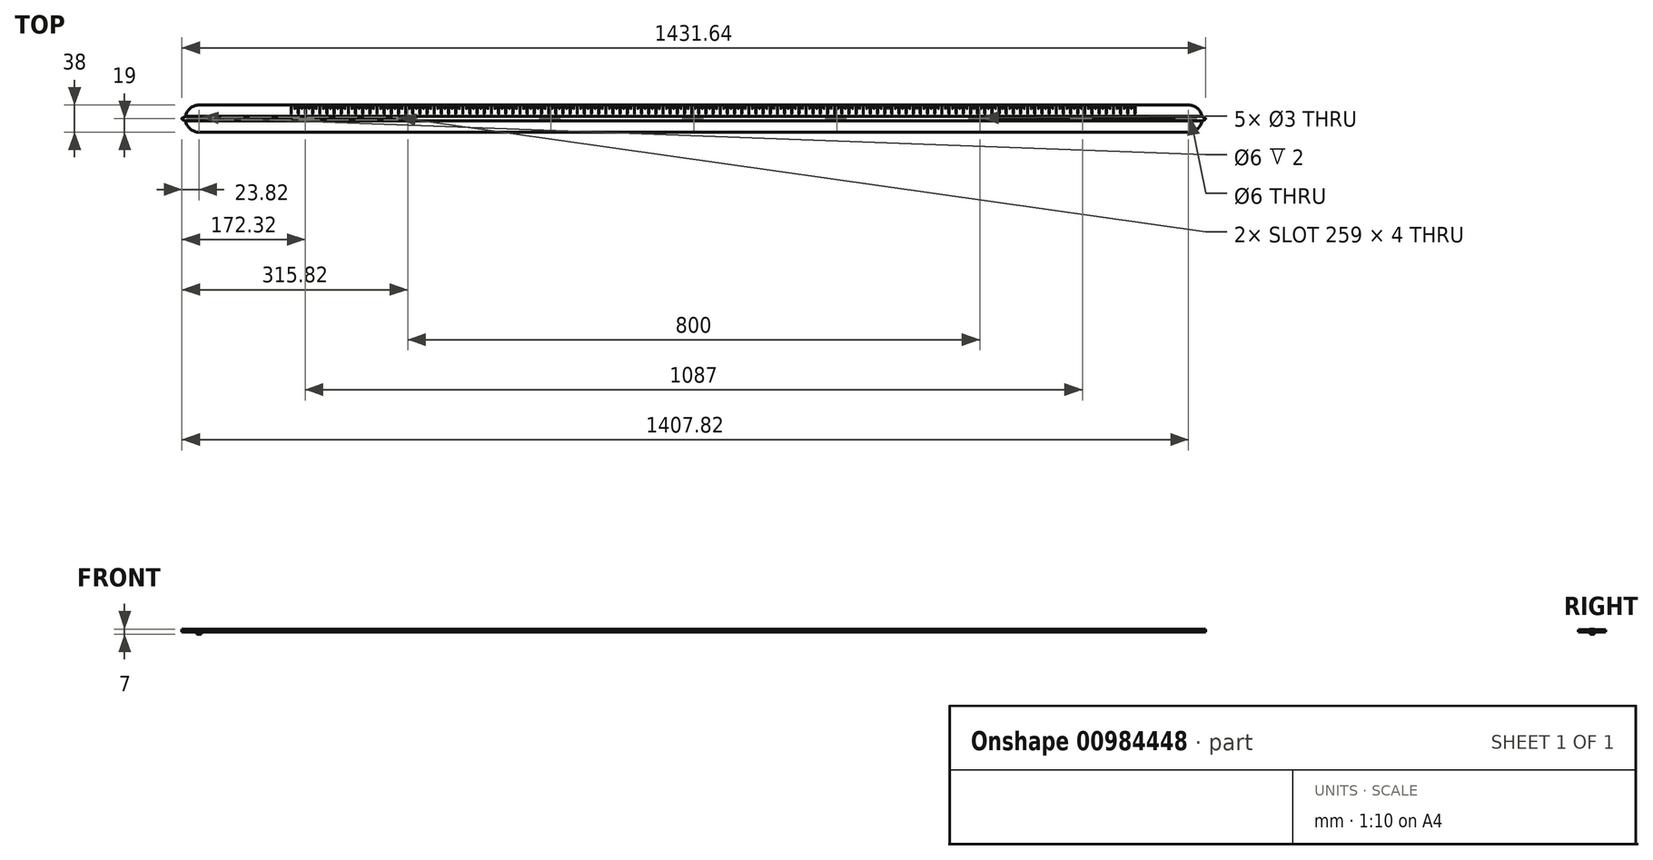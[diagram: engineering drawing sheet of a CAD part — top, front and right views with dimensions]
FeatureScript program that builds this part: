
annotation { "Feature Type Name" : "Feature", "Feature Type Description" : "" }
export const myFeature = defineFeature(function(context is Context, id is Id, definition is map)
    precondition{}
    {
        {
            var Q0;
            Q0=qCreatedBy(makeId("Right.planeOp"),FACE);
            var sketch = newSketch(context, id + "F0", { "sketchPlane" : qUnion([Q0])});
            skLineSegment(sketch, "E0", {"start": v(0, 0) * mm, "end": v(-19, 0) * mm, "construction": true});
            skLineSegment(sketch, "E1", {"start": v(-19, 0) * mm, "end": v(19, 0) * mm});
            skLineSegment(sketch, "E2", {"start": v(19, 0) * mm, "end": v(19, 3) * mm});
            skLineSegment(sketch, "E3", {"start": v(19, 3) * mm, "end": v(3.25, 3) * mm});
            skLineSegment(sketch, "E4", {"start": v(3.25, 3) * mm, "end": v(3.25, 4) * mm, "construction": true});
            skLineSegment(sketch, "E5", {"start": v(3.25, 4) * mm, "end": v(0, 4) * mm, "construction": true});
            skLineSegment(sketch, "E6", {"start": v(0, 4) * mm, "end": v(3, 4) * mm, "construction": true});
            skLineSegment(sketch, "E7", {"start": v(3, 4) * mm, "end": v(3.25, 3) * mm});
            skLineSegment(sketch, "E8", {"start": v(3, 4) * mm, "end": v(-3, 4) * mm});
            skLineSegment(sketch, "E9", {"start": v(-19, 0) * mm, "end": v(-19, 3) * mm});
            skLineSegment(sketch, "E10", {"start": v(-19, 3) * mm, "end": v(-3.25, 3) * mm});
            skLineSegment(sketch, "E11", {"start": v(-3.25, 3) * mm, "end": v(-3, 4) * mm});
            skSolve(sketch);
        }
        {
            var Q0;
            Q0=makeQuery(id+"F0.imprint","IMPRINT",FACE,{"disambiguationData":[TD([[makeQuery(id+"F0.imprint","IMPRINT",EDGE,{"derivedFrom":sQuery(id+"F0.wireOp",EDGE,"E1")}),1.0]])]});
            extrude(context, id + "F1", {"entities" : qUnion([Q0]), "depth" : 1280 * mm, "offsetDistance" : 25 * mm, "hasSecondDirection" : true, "secondDirectionOppositeDirection" : true, "secondDirectionDepth" : (129 + 19 + 6) * mm});
        }
        {
            var Q0;
            Q0=qCreatedBy(makeId("Top.planeOp"),FACE);
            var sketch = newSketch(context, id + "F2", { "sketchPlane" : qUnion([Q0])});
            skLineSegment(sketch, "E12.0.0", {"start": v(-154, 3) * mm, "end": v(-154, -3) * mm, "construction": true});
            skLineSegment(sketch, "E12.0.1", {"start": v(-154, -3) * mm, "end": v(1280, -3) * mm, "construction": true});
            skLineSegment(sketch, "E12.0.2", {"start": v(1280, -3) * mm, "end": v(1280, 3) * mm, "construction": true});
            skLineSegment(sketch, "E12.0.3", {"start": v(1280, 3) * mm, "end": v(-154, 3) * mm, "construction": true});
            skLineSegment(sketch, "E13", {"start": v(563, 3) * mm, "end": v(563, -3) * mm});
            skSolve(sketch);
        }
        {
            var Q0;
            Q0=qCreatedBy(makeId("Top.planeOp"),FACE);
            var sketch = newSketch(context, id + "F3", { "sketchPlane" : qUnion([Q0])});
            skLineSegment(sketch, "E14", {"start": v(0, 0) * mm, "end": v(-129, 0) * mm, "construction": true});
            skCircle(sketch, "E15", {"center": v(-129, 0) * mm, "radius": 3 * mm});
            skCircle(sketch, "E16.MirrorC", {"center": v(1255, 0) * mm, "radius": 3 * mm});
            skLineSegment(sketch, "E17.MirrorCS", {"start": v(1126, 0) * mm, "end": v(1255, 0) * mm, "construction": true});
            skSolve(sketch);
        }
        {
            var Q0;
            Q0 = qSketchRegion(id + "F3", true);
            extrude(context, id + "F4", {"entities" : qUnion([Q0]), "operationType" : NewBodyOperationType.REMOVE, "depth" : 25 * mm, "offsetDistance" : 25 * mm});
        }
        {
            var Q0;
            Q0=qCreatedBy(makeId("Top.planeOp"),FACE);
            var sketch = newSketch(context, id + "F5", { "sketchPlane" : qUnion([Q0])});
            skArc(sketch, "E18.0", {"start": v(-129, 3) * mm, "mid": v(-132, 0) * mm, "end": v(-129, -3) * mm, "construction": true});
            skArc(sketch, "E19.0", {"start": v(-129, -3) * mm, "mid": v(-126, 0) * mm, "end": v(-129, 3) * mm, "construction": true});
            skLineSegment(sketch, "E20", {"start": v(-129, 0) * mm, "end": v(-108, 0) * mm, "construction": true});
            skPoint(sketch, "E20.endSnap0", {"position": v(-126, 0) * mm});
            skLineSegment(sketch, "E21", {"start": v(-108, 0) * mm, "end": v(147, 0) * mm});
            skArc(sketch, "E22.0.startCap", {"start": v(-108, -2) * mm, "mid": v(-110, 0) * mm, "end": v(-108, 2) * mm});
            skArc(sketch, "E22.0.endCap", {"start": v(147, 2) * mm, "mid": v(149, 0) * mm, "end": v(147, -2) * mm});
            skLineSegment(sketch, "E22.0.left", {"start": v(-108, 2) * mm, "end": v(147, 2) * mm});
            skLineSegment(sketch, "E22.0.right", {"start": v(-108, -2) * mm, "end": v(147, -2) * mm});
            skArc(sketch, "E23.MirrorCS", {"start": v(1255, -3) * mm, "mid": v(1252, 0) * mm, "end": v(1255, 3) * mm, "construction": true});
            skArc(sketch, "E24.MirrorCS", {"start": v(1234, -2) * mm, "mid": v(1236, 0) * mm, "end": v(1234, 2) * mm});
            skArc(sketch, "E25.MirrorCS", {"start": v(1255, 3) * mm, "mid": v(1258, 0) * mm, "end": v(1255, -3) * mm, "construction": true});
            skPoint(sketch, "E26.MirrorP", {"position": v(1252, 0) * mm});
            skLineSegment(sketch, "E27.MirrorCS", {"start": v(1255, 0) * mm, "end": v(1234, 0) * mm, "construction": true});
            skArc(sketch, "E28.MirrorCS", {"start": v(979, 2) * mm, "mid": v(977, 0) * mm, "end": v(979, -2) * mm});
            skLineSegment(sketch, "E29.MirrorCS", {"start": v(1234, 0) * mm, "end": v(979, 0) * mm});
            skLineSegment(sketch, "E30.MirrorCS", {"start": v(1234, -2) * mm, "end": v(979, -2) * mm});
            skLineSegment(sketch, "E31.MirrorCS", {"start": v(1234, 2) * mm, "end": v(979, 2) * mm});
            skSolve(sketch);
        }
        {
            var Q0;
            Q0 = qSketchRegion(id + "F5", true);
            extrude(context, id + "F6", {"entities" : qUnion([Q0]), "operationType" : NewBodyOperationType.REMOVE, "depth" : 25 * mm, "offsetDistance" : 25 * mm});
        }
        {
            var Q0;
            Q0=qCreatedBy(makeId("Top.planeOp"),FACE);
            var sketch = newSketch(context, id + "F7", { "sketchPlane" : qUnion([Q0])});
            skArc(sketch, "E32.0", {"start": v(-129, 3) * mm, "mid": v(-132, 0) * mm, "end": v(-129, -3) * mm, "construction": true});
            skArc(sketch, "E33", {"start": v(-129, 19) * mm, "mid": v(-140.88, 14.83) * mm, "end": v(-147.54, 4.15) * mm});
            skLineSegment(sketch, "E34.0", {"start": v(1280, 3.25) * mm, "end": v(-154, 3.25) * mm, "construction": true});
            skLineSegment(sketch, "E35.0", {"start": v(1280, -3.25) * mm, "end": v(-154, -3.25) * mm, "construction": true});
            skLineSegment(sketch, "E36.0", {"start": v(-154, 3) * mm, "end": v(-154, -3) * mm, "construction": true});
            skLineSegment(sketch, "E37", {"start": v(-152.28, 0.89) * mm, "end": v(-148.57, 2.8) * mm});
            skLineSegment(sketch, "E38.bottom", {"start": v(-158.98, 22.26) * mm, "end": v(-129, 22.26) * mm});
            skLineSegment(sketch, "E38.top", {"start": v(-158.98, -20.88) * mm, "end": v(-129, -20.88) * mm});
            skLineSegment(sketch, "E38.left", {"start": v(-158.98, 22.26) * mm, "end": v(-158.98, -20.88) * mm});
            skLineSegment(sketch, "E38.right", {"start": v(-129, 22.26) * mm, "end": v(-129, 19) * mm});
            skLineSegment(sketch, "E39.trimOffspring", {"start": v(-129, -19) * mm, "end": v(-129, -20.88) * mm});
            skLineSegment(sketch, "E40.trimOffspring", {"start": v(-129, -3) * mm, "end": v(-129, -3.25) * mm});
            skLineSegment(sketch, "E41.trimOffspring", {"start": v(-129, 3.25) * mm, "end": v(-129, 3) * mm});
            skLineSegment(sketch, "E42", {"start": v(-152.28, -0.89) * mm, "end": v(-148.57, -2.8) * mm});
            skArc(sketch, "E43.trimOffspring", {"start": v(-147.54, -4.15) * mm, "mid": v(-140.88, -14.83) * mm, "end": v(-129, -19) * mm});
            skLineSegment(sketch, "E44", {"start": v(-129, 0) * mm, "end": v(-154, 0) * mm, "construction": true});
            skPoint(sketch, "E45.visualSharp", {"position": v(-147.72, 3.25) * mm});
            skArc(sketch, "E45.filletArc", {"start": v(-148.57, 2.8) * mm, "mid": v(-147.9, 3.36) * mm, "end": v(-147.54, 4.15) * mm});
            skPoint(sketch, "E46.visualSharp", {"position": v(-147.72, -3.25) * mm});
            skArc(sketch, "E46.filletArc", {"start": v(-147.54, -4.15) * mm, "mid": v(-147.9, -3.36) * mm, "end": v(-148.57, -2.8) * mm});
            skPoint(sketch, "E47.visualSharp", {"position": v(-154, 0) * mm});
            skArc(sketch, "E47.filletArc", {"start": v(-152.28, 0.89) * mm, "mid": v(-152.82, 0) * mm, "end": v(-152.28, -0.89) * mm});
            skArc(sketch, "E48.MirrorCS", {"start": v(1278.28, 0.89) * mm, "mid": v(1278.82, 0) * mm, "end": v(1278.28, -0.89) * mm});
            skArc(sketch, "E49.MirrorCS", {"start": v(1274.57, 2.8) * mm, "mid": v(1273.9, 3.36) * mm, "end": v(1273.54, 4.15) * mm});
            skLineSegment(sketch, "E50.MirrorCS", {"start": v(1278.28, -0.89) * mm, "end": v(1274.57, -2.8) * mm});
            skLineSegment(sketch, "E51.MirrorCS", {"start": v(1278.28, 0.89) * mm, "end": v(1274.57, 2.8) * mm});
            skLineSegment(sketch, "E52.MirrorCS", {"start": v(1280, 3) * mm, "end": v(1280, -3) * mm, "construction": true});
            skArc(sketch, "E53.MirrorCS", {"start": v(1273.54, -4.15) * mm, "mid": v(1273.9, -3.36) * mm, "end": v(1274.57, -2.8) * mm});
            skLineSegment(sketch, "E54.MirrorCS", {"start": v(1255, 3.25) * mm, "end": v(1255, 3) * mm});
            skLineSegment(sketch, "E55.MirrorCS", {"start": v(1255, -3) * mm, "end": v(1255, -3.25) * mm});
            skLineSegment(sketch, "E56.MirrorCS", {"start": v(1255, 0) * mm, "end": v(1280, 0) * mm, "construction": true});
            skArc(sketch, "E57.MirrorCS", {"start": v(1255, 3) * mm, "mid": v(1258, 0) * mm, "end": v(1255, -3) * mm, "construction": true});
            skLineSegment(sketch, "E58.MirrorCS", {"start": v(1255, -19) * mm, "end": v(1255, -20.88) * mm});
            skArc(sketch, "E59.MirrorCS", {"start": v(1273.54, -4.15) * mm, "mid": v(1266.88, -14.83) * mm, "end": v(1255, -19) * mm});
            skLineSegment(sketch, "E60.MirrorCS", {"start": v(1255, 22.26) * mm, "end": v(1255, 19) * mm});
            skArc(sketch, "E61.MirrorCS", {"start": v(1255, 19) * mm, "mid": v(1266.88, 14.83) * mm, "end": v(1273.54, 4.15) * mm});
            skLineSegment(sketch, "E62.MirrorCS", {"start": v(1284.98, 22.26) * mm, "end": v(1284.98, -20.88) * mm});
            skLineSegment(sketch, "E63.MirrorCS", {"start": v(1284.98, -20.88) * mm, "end": v(1255, -20.88) * mm});
            skLineSegment(sketch, "E64.MirrorCS", {"start": v(1284.98, 22.26) * mm, "end": v(1255, 22.26) * mm});
            skPoint(sketch, "E65.MirrorP", {"position": v(1273.72, 3.25) * mm});
            skPoint(sketch, "E66.MirrorP", {"position": v(1273.72, -3.25) * mm});
            skPoint(sketch, "E67.MirrorP", {"position": v(1280, 0) * mm});
            skSolve(sketch);
        }
        {
            var Q0;
            Q0 = qSketchRegion(id + "F7", true);
            extrude(context, id + "F8", {"entities" : qUnion([Q0]), "operationType" : NewBodyOperationType.REMOVE, "depth" : 25 * mm, "offsetDistance" : 25 * mm});
        }
        {
            var Q0;
            Q0=qCreatedBy(makeId("Top.planeOp"),FACE);
            var sketch = newSketch(context, id + "F9", { "sketchPlane" : qUnion([Q0])});
            skArc(sketch, "E68.0", {"start": v(147, 2) * mm, "mid": v(149, 0) * mm, "end": v(147, -2) * mm, "construction": true});
            skArc(sketch, "E69.0", {"start": v(979, 2) * mm, "mid": v(977, 0) * mm, "end": v(979, -2) * mm, "construction": true});
            skLineSegment(sketch, "E70", {"start": v(147, 0) * mm, "end": v(979, 0) * mm, "construction": true});
            skCircle(sketch, "E71", {"center": v(563, 0) * mm, "radius": 1.5 * mm});
            skCircle(sketch, "E72.1.0.0", {"center": v(763, 0) * mm, "radius": 1.5 * mm});
            skCircle(sketch, "E72.2.0.0", {"center": v(963, 0) * mm, "radius": 1.5 * mm});
            skLineSegment(sketch, "E72.direction1", {"start": v(563, 0) * mm, "end": v(763, 0) * mm, "construction": true});
            skCircle(sketch, "E73.1.0.0", {"center": v(363, 0) * mm, "radius": 1.5 * mm});
            skCircle(sketch, "E73.2.0.0", {"center": v(163, 0) * mm, "radius": 1.5 * mm});
            skLineSegment(sketch, "E73.direction1", {"start": v(563, 0) * mm, "end": v(363, 0) * mm, "construction": true});
            skSolve(sketch);
        }
        {
            var Q0;
            Q0 = qSketchRegion(id + "F9", true);
            extrude(context, id + "F10", {"entities" : qUnion([Q0]), "operationType" : NewBodyOperationType.REMOVE, "depth" : 25 * mm, "offsetDistance" : 25 * mm});
        }
        {
            var Q0;
            Q0=makeQuery(id+"F1.opExtrude","SWEPT_FACE",FACE,{"disambiguationData":[OSD([sQuery(id+"F0.wireOp",EDGE,"E3")])]});
            var sketch = newSketch(context, id + "F11", { "sketchPlane" : qUnion([Q0])});
            skLineSegment(sketch, "E74", {"start": v(0, 0) * mm, "end": v(0, 19) * mm, "construction": true});
            skLineSegment(sketch, "E75", {"start": v(0, 19) * mm, "end": v(0, 7) * mm});
            skArc(sketch, "E76.0.startCap", {"start": v(-0.25, 19) * mm, "mid": v(0, 19.25) * mm, "end": v(0.25, 19) * mm});
            skArc(sketch, "E76.0.endCap", {"start": v(0.25, 7) * mm, "mid": v(0, 6.75) * mm, "end": v(-0.25, 7) * mm});
            skLineSegment(sketch, "E76.0.left", {"start": v(0.25, 19) * mm, "end": v(0.25, 7) * mm});
            skLineSegment(sketch, "E76.0.right", {"start": v(-0.25, 19) * mm, "end": v(-0.25, 7) * mm});
            skLineSegment(sketch, "E77.1.0.0", {"start": v(10.25, 19) * mm, "end": v(10.25, 7) * mm});
            skLineSegment(sketch, "E77.1.0.1", {"start": v(9.75, 19) * mm, "end": v(9.75, 7) * mm});
            skLineSegment(sketch, "E77.1.0.2", {"start": v(10, 19) * mm, "end": v(10, 7) * mm});
            skArc(sketch, "E77.1.0.3", {"start": v(10.25, 7) * mm, "mid": v(10, 6.75) * mm, "end": v(9.75, 7) * mm});
            skArc(sketch, "E77.1.0.4", {"start": v(9.75, 19) * mm, "mid": v(10, 19.25) * mm, "end": v(10.25, 19) * mm});
            skLineSegment(sketch, "E77.2.0.0", {"start": v(20.25, 19) * mm, "end": v(20.25, 7) * mm});
            skLineSegment(sketch, "E77.2.0.1", {"start": v(19.75, 19) * mm, "end": v(19.75, 7) * mm});
            skLineSegment(sketch, "E77.2.0.2", {"start": v(20, 19) * mm, "end": v(20, 7) * mm});
            skArc(sketch, "E77.2.0.3", {"start": v(20.25, 7) * mm, "mid": v(20, 6.75) * mm, "end": v(19.75, 7) * mm});
            skArc(sketch, "E77.2.0.4", {"start": v(19.75, 19) * mm, "mid": v(20, 19.25) * mm, "end": v(20.25, 19) * mm});
            skLineSegment(sketch, "E77.3.0.0", {"start": v(30.25, 19) * mm, "end": v(30.25, 7) * mm});
            skLineSegment(sketch, "E77.3.0.1", {"start": v(29.75, 19) * mm, "end": v(29.75, 7) * mm});
            skLineSegment(sketch, "E77.3.0.2", {"start": v(30, 19) * mm, "end": v(30, 7) * mm});
            skArc(sketch, "E77.3.0.3", {"start": v(30.25, 7) * mm, "mid": v(30, 6.75) * mm, "end": v(29.75, 7) * mm});
            skArc(sketch, "E77.3.0.4", {"start": v(29.75, 19) * mm, "mid": v(30, 19.25) * mm, "end": v(30.25, 19) * mm});
            skLineSegment(sketch, "E77.4.0.0", {"start": v(40.25, 19) * mm, "end": v(40.25, 7) * mm});
            skLineSegment(sketch, "E77.4.0.1", {"start": v(39.75, 19) * mm, "end": v(39.75, 7) * mm});
            skLineSegment(sketch, "E77.4.0.2", {"start": v(40, 19) * mm, "end": v(40, 7) * mm});
            skArc(sketch, "E77.4.0.3", {"start": v(40.25, 7) * mm, "mid": v(40, 6.75) * mm, "end": v(39.75, 7) * mm});
            skArc(sketch, "E77.4.0.4", {"start": v(39.75, 19) * mm, "mid": v(40, 19.25) * mm, "end": v(40.25, 19) * mm});
            skLineSegment(sketch, "E77.5.0.0", {"start": v(50.25, 19) * mm, "end": v(50.25, 7) * mm});
            skLineSegment(sketch, "E77.5.0.1", {"start": v(49.75, 19) * mm, "end": v(49.75, 7) * mm});
            skLineSegment(sketch, "E77.5.0.2", {"start": v(50, 19) * mm, "end": v(50, 7) * mm});
            skArc(sketch, "E77.5.0.3", {"start": v(50.25, 7) * mm, "mid": v(50, 6.75) * mm, "end": v(49.75, 7) * mm});
            skArc(sketch, "E77.5.0.4", {"start": v(49.75, 19) * mm, "mid": v(50, 19.25) * mm, "end": v(50.25, 19) * mm});
            skLineSegment(sketch, "E77.6.0.0", {"start": v(60.25, 19) * mm, "end": v(60.25, 7) * mm});
            skLineSegment(sketch, "E77.6.0.1", {"start": v(59.75, 19) * mm, "end": v(59.75, 7) * mm});
            skLineSegment(sketch, "E77.6.0.2", {"start": v(60, 19) * mm, "end": v(60, 7) * mm});
            skArc(sketch, "E77.6.0.3", {"start": v(60.25, 7) * mm, "mid": v(60, 6.75) * mm, "end": v(59.75, 7) * mm});
            skArc(sketch, "E77.6.0.4", {"start": v(59.75, 19) * mm, "mid": v(60, 19.25) * mm, "end": v(60.25, 19) * mm});
            skLineSegment(sketch, "E77.7.0.0", {"start": v(70.25, 19) * mm, "end": v(70.25, 7) * mm});
            skLineSegment(sketch, "E77.7.0.1", {"start": v(69.75, 19) * mm, "end": v(69.75, 7) * mm});
            skLineSegment(sketch, "E77.7.0.2", {"start": v(70, 19) * mm, "end": v(70, 7) * mm});
            skArc(sketch, "E77.7.0.3", {"start": v(70.25, 7) * mm, "mid": v(70, 6.75) * mm, "end": v(69.75, 7) * mm});
            skArc(sketch, "E77.7.0.4", {"start": v(69.75, 19) * mm, "mid": v(70, 19.25) * mm, "end": v(70.25, 19) * mm});
            skLineSegment(sketch, "E77.8.0.0", {"start": v(80.25, 19) * mm, "end": v(80.25, 7) * mm});
            skLineSegment(sketch, "E77.8.0.1", {"start": v(79.75, 19) * mm, "end": v(79.75, 7) * mm});
            skLineSegment(sketch, "E77.8.0.2", {"start": v(80, 19) * mm, "end": v(80, 7) * mm});
            skArc(sketch, "E77.8.0.3", {"start": v(80.25, 7) * mm, "mid": v(80, 6.75) * mm, "end": v(79.75, 7) * mm});
            skArc(sketch, "E77.8.0.4", {"start": v(79.75, 19) * mm, "mid": v(80, 19.25) * mm, "end": v(80.25, 19) * mm});
            skLineSegment(sketch, "E77.9.0.0", {"start": v(90.25, 19) * mm, "end": v(90.25, 7) * mm});
            skLineSegment(sketch, "E77.9.0.1", {"start": v(89.75, 19) * mm, "end": v(89.75, 7) * mm});
            skLineSegment(sketch, "E77.9.0.2", {"start": v(90, 19) * mm, "end": v(90, 7) * mm});
            skArc(sketch, "E77.9.0.3", {"start": v(90.25, 7) * mm, "mid": v(90, 6.75) * mm, "end": v(89.75, 7) * mm});
            skArc(sketch, "E77.9.0.4", {"start": v(89.75, 19) * mm, "mid": v(90, 19.25) * mm, "end": v(90.25, 19) * mm});
            skLineSegment(sketch, "E77.10.0.0", {"start": v(100.25, 19) * mm, "end": v(100.25, 7) * mm});
            skLineSegment(sketch, "E77.10.0.1", {"start": v(99.75, 19) * mm, "end": v(99.75, 7) * mm});
            skLineSegment(sketch, "E77.10.0.2", {"start": v(100, 19) * mm, "end": v(100, 7) * mm});
            skArc(sketch, "E77.10.0.3", {"start": v(100.25, 7) * mm, "mid": v(100, 6.75) * mm, "end": v(99.75, 7) * mm});
            skArc(sketch, "E77.10.0.4", {"start": v(99.75, 19) * mm, "mid": v(100, 19.25) * mm, "end": v(100.25, 19) * mm});
            skLineSegment(sketch, "E77.11.0.0", {"start": v(110.25, 19) * mm, "end": v(110.25, 7) * mm});
            skLineSegment(sketch, "E77.11.0.1", {"start": v(109.75, 19) * mm, "end": v(109.75, 7) * mm});
            skLineSegment(sketch, "E77.11.0.2", {"start": v(110, 19) * mm, "end": v(110, 7) * mm});
            skArc(sketch, "E77.11.0.3", {"start": v(110.25, 7) * mm, "mid": v(110, 6.75) * mm, "end": v(109.75, 7) * mm});
            skArc(sketch, "E77.11.0.4", {"start": v(109.75, 19) * mm, "mid": v(110, 19.25) * mm, "end": v(110.25, 19) * mm});
            skLineSegment(sketch, "E77.12.0.0", {"start": v(120.25, 19) * mm, "end": v(120.25, 7) * mm});
            skLineSegment(sketch, "E77.12.0.1", {"start": v(119.75, 19) * mm, "end": v(119.75, 7) * mm});
            skLineSegment(sketch, "E77.12.0.2", {"start": v(120, 19) * mm, "end": v(120, 7) * mm});
            skArc(sketch, "E77.12.0.3", {"start": v(120.25, 7) * mm, "mid": v(120, 6.75) * mm, "end": v(119.75, 7) * mm});
            skArc(sketch, "E77.12.0.4", {"start": v(119.75, 19) * mm, "mid": v(120, 19.25) * mm, "end": v(120.25, 19) * mm});
            skLineSegment(sketch, "E77.13.0.0", {"start": v(130.25, 19) * mm, "end": v(130.25, 7) * mm});
            skLineSegment(sketch, "E77.13.0.1", {"start": v(129.75, 19) * mm, "end": v(129.75, 7) * mm});
            skLineSegment(sketch, "E77.13.0.2", {"start": v(130, 19) * mm, "end": v(130, 7) * mm});
            skArc(sketch, "E77.13.0.3", {"start": v(130.25, 7) * mm, "mid": v(130, 6.75) * mm, "end": v(129.75, 7) * mm});
            skArc(sketch, "E77.13.0.4", {"start": v(129.75, 19) * mm, "mid": v(130, 19.25) * mm, "end": v(130.25, 19) * mm});
            skLineSegment(sketch, "E77.14.0.0", {"start": v(140.25, 19) * mm, "end": v(140.25, 7) * mm});
            skLineSegment(sketch, "E77.14.0.1", {"start": v(139.75, 19) * mm, "end": v(139.75, 7) * mm});
            skLineSegment(sketch, "E77.14.0.2", {"start": v(140, 19) * mm, "end": v(140, 7) * mm});
            skArc(sketch, "E77.14.0.3", {"start": v(140.25, 7) * mm, "mid": v(140, 6.75) * mm, "end": v(139.75, 7) * mm});
            skArc(sketch, "E77.14.0.4", {"start": v(139.75, 19) * mm, "mid": v(140, 19.25) * mm, "end": v(140.25, 19) * mm});
            skLineSegment(sketch, "E77.15.0.0", {"start": v(150.25, 19) * mm, "end": v(150.25, 7) * mm});
            skLineSegment(sketch, "E77.15.0.1", {"start": v(149.75, 19) * mm, "end": v(149.75, 7) * mm});
            skLineSegment(sketch, "E77.15.0.2", {"start": v(150, 19) * mm, "end": v(150, 7) * mm});
            skArc(sketch, "E77.15.0.3", {"start": v(150.25, 7) * mm, "mid": v(150, 6.75) * mm, "end": v(149.75, 7) * mm});
            skArc(sketch, "E77.15.0.4", {"start": v(149.75, 19) * mm, "mid": v(150, 19.25) * mm, "end": v(150.25, 19) * mm});
            skLineSegment(sketch, "E77.16.0.0", {"start": v(160.25, 19) * mm, "end": v(160.25, 7) * mm});
            skLineSegment(sketch, "E77.16.0.1", {"start": v(159.75, 19) * mm, "end": v(159.75, 7) * mm});
            skLineSegment(sketch, "E77.16.0.2", {"start": v(160, 19) * mm, "end": v(160, 7) * mm});
            skArc(sketch, "E77.16.0.3", {"start": v(160.25, 7) * mm, "mid": v(160, 6.75) * mm, "end": v(159.75, 7) * mm});
            skArc(sketch, "E77.16.0.4", {"start": v(159.75, 19) * mm, "mid": v(160, 19.25) * mm, "end": v(160.25, 19) * mm});
            skLineSegment(sketch, "E77.17.0.0", {"start": v(170.25, 19) * mm, "end": v(170.25, 7) * mm});
            skLineSegment(sketch, "E77.17.0.1", {"start": v(169.75, 19) * mm, "end": v(169.75, 7) * mm});
            skLineSegment(sketch, "E77.17.0.2", {"start": v(170, 19) * mm, "end": v(170, 7) * mm});
            skArc(sketch, "E77.17.0.3", {"start": v(170.25, 7) * mm, "mid": v(170, 6.75) * mm, "end": v(169.75, 7) * mm});
            skArc(sketch, "E77.17.0.4", {"start": v(169.75, 19) * mm, "mid": v(170, 19.25) * mm, "end": v(170.25, 19) * mm});
            skLineSegment(sketch, "E77.18.0.0", {"start": v(180.25, 19) * mm, "end": v(180.25, 7) * mm});
            skLineSegment(sketch, "E77.18.0.1", {"start": v(179.75, 19) * mm, "end": v(179.75, 7) * mm});
            skLineSegment(sketch, "E77.18.0.2", {"start": v(180, 19) * mm, "end": v(180, 7) * mm});
            skArc(sketch, "E77.18.0.3", {"start": v(180.25, 7) * mm, "mid": v(180, 6.75) * mm, "end": v(179.75, 7) * mm});
            skArc(sketch, "E77.18.0.4", {"start": v(179.75, 19) * mm, "mid": v(180, 19.25) * mm, "end": v(180.25, 19) * mm});
            skLineSegment(sketch, "E77.19.0.0", {"start": v(190.25, 19) * mm, "end": v(190.25, 7) * mm});
            skLineSegment(sketch, "E77.19.0.1", {"start": v(189.75, 19) * mm, "end": v(189.75, 7) * mm});
            skLineSegment(sketch, "E77.19.0.2", {"start": v(190, 19) * mm, "end": v(190, 7) * mm});
            skArc(sketch, "E77.19.0.3", {"start": v(190.25, 7) * mm, "mid": v(190, 6.75) * mm, "end": v(189.75, 7) * mm});
            skArc(sketch, "E77.19.0.4", {"start": v(189.75, 19) * mm, "mid": v(190, 19.25) * mm, "end": v(190.25, 19) * mm});
            skLineSegment(sketch, "E77.20.0.0", {"start": v(200.25, 19) * mm, "end": v(200.25, 7) * mm});
            skLineSegment(sketch, "E77.20.0.1", {"start": v(199.75, 19) * mm, "end": v(199.75, 7) * mm});
            skLineSegment(sketch, "E77.20.0.2", {"start": v(200, 19) * mm, "end": v(200, 7) * mm});
            skArc(sketch, "E77.20.0.3", {"start": v(200.25, 7) * mm, "mid": v(200, 6.75) * mm, "end": v(199.75, 7) * mm});
            skArc(sketch, "E77.20.0.4", {"start": v(199.75, 19) * mm, "mid": v(200, 19.25) * mm, "end": v(200.25, 19) * mm});
            skLineSegment(sketch, "E77.21.0.0", {"start": v(210.25, 19) * mm, "end": v(210.25, 7) * mm});
            skLineSegment(sketch, "E77.21.0.1", {"start": v(209.75, 19) * mm, "end": v(209.75, 7) * mm});
            skLineSegment(sketch, "E77.21.0.2", {"start": v(210, 19) * mm, "end": v(210, 7) * mm});
            skArc(sketch, "E77.21.0.3", {"start": v(210.25, 7) * mm, "mid": v(210, 6.75) * mm, "end": v(209.75, 7) * mm});
            skArc(sketch, "E77.21.0.4", {"start": v(209.75, 19) * mm, "mid": v(210, 19.25) * mm, "end": v(210.25, 19) * mm});
            skLineSegment(sketch, "E77.22.0.0", {"start": v(220.25, 19) * mm, "end": v(220.25, 7) * mm});
            skLineSegment(sketch, "E77.22.0.1", {"start": v(219.75, 19) * mm, "end": v(219.75, 7) * mm});
            skLineSegment(sketch, "E77.22.0.2", {"start": v(220, 19) * mm, "end": v(220, 7) * mm});
            skArc(sketch, "E77.22.0.3", {"start": v(220.25, 7) * mm, "mid": v(220, 6.75) * mm, "end": v(219.75, 7) * mm});
            skArc(sketch, "E77.22.0.4", {"start": v(219.75, 19) * mm, "mid": v(220, 19.25) * mm, "end": v(220.25, 19) * mm});
            skLineSegment(sketch, "E77.23.0.0", {"start": v(230.25, 19) * mm, "end": v(230.25, 7) * mm});
            skLineSegment(sketch, "E77.23.0.1", {"start": v(229.75, 19) * mm, "end": v(229.75, 7) * mm});
            skLineSegment(sketch, "E77.23.0.2", {"start": v(230, 19) * mm, "end": v(230, 7) * mm});
            skArc(sketch, "E77.23.0.3", {"start": v(230.25, 7) * mm, "mid": v(230, 6.75) * mm, "end": v(229.75, 7) * mm});
            skArc(sketch, "E77.23.0.4", {"start": v(229.75, 19) * mm, "mid": v(230, 19.25) * mm, "end": v(230.25, 19) * mm});
            skLineSegment(sketch, "E77.24.0.0", {"start": v(240.25, 19) * mm, "end": v(240.25, 7) * mm});
            skLineSegment(sketch, "E77.24.0.1", {"start": v(239.75, 19) * mm, "end": v(239.75, 7) * mm});
            skLineSegment(sketch, "E77.24.0.2", {"start": v(240, 19) * mm, "end": v(240, 7) * mm});
            skArc(sketch, "E77.24.0.3", {"start": v(240.25, 7) * mm, "mid": v(240, 6.75) * mm, "end": v(239.75, 7) * mm});
            skArc(sketch, "E77.24.0.4", {"start": v(239.75, 19) * mm, "mid": v(240, 19.25) * mm, "end": v(240.25, 19) * mm});
            skLineSegment(sketch, "E77.25.0.0", {"start": v(250.25, 19) * mm, "end": v(250.25, 7) * mm});
            skLineSegment(sketch, "E77.25.0.1", {"start": v(249.75, 19) * mm, "end": v(249.75, 7) * mm});
            skLineSegment(sketch, "E77.25.0.2", {"start": v(250, 19) * mm, "end": v(250, 7) * mm});
            skArc(sketch, "E77.25.0.3", {"start": v(250.25, 7) * mm, "mid": v(250, 6.75) * mm, "end": v(249.75, 7) * mm});
            skArc(sketch, "E77.25.0.4", {"start": v(249.75, 19) * mm, "mid": v(250, 19.25) * mm, "end": v(250.25, 19) * mm});
            skLineSegment(sketch, "E77.26.0.0", {"start": v(260.25, 19) * mm, "end": v(260.25, 7) * mm});
            skLineSegment(sketch, "E77.26.0.1", {"start": v(259.75, 19) * mm, "end": v(259.75, 7) * mm});
            skLineSegment(sketch, "E77.26.0.2", {"start": v(260, 19) * mm, "end": v(260, 7) * mm});
            skArc(sketch, "E77.26.0.3", {"start": v(260.25, 7) * mm, "mid": v(260, 6.75) * mm, "end": v(259.75, 7) * mm});
            skArc(sketch, "E77.26.0.4", {"start": v(259.75, 19) * mm, "mid": v(260, 19.25) * mm, "end": v(260.25, 19) * mm});
            skLineSegment(sketch, "E77.27.0.0", {"start": v(270.25, 19) * mm, "end": v(270.25, 7) * mm});
            skLineSegment(sketch, "E77.27.0.1", {"start": v(269.75, 19) * mm, "end": v(269.75, 7) * mm});
            skLineSegment(sketch, "E77.27.0.2", {"start": v(270, 19) * mm, "end": v(270, 7) * mm});
            skArc(sketch, "E77.27.0.3", {"start": v(270.25, 7) * mm, "mid": v(270, 6.75) * mm, "end": v(269.75, 7) * mm});
            skArc(sketch, "E77.27.0.4", {"start": v(269.75, 19) * mm, "mid": v(270, 19.25) * mm, "end": v(270.25, 19) * mm});
            skLineSegment(sketch, "E77.28.0.0", {"start": v(280.25, 19) * mm, "end": v(280.25, 7) * mm});
            skLineSegment(sketch, "E77.28.0.1", {"start": v(279.75, 19) * mm, "end": v(279.75, 7) * mm});
            skLineSegment(sketch, "E77.28.0.2", {"start": v(280, 19) * mm, "end": v(280, 7) * mm});
            skArc(sketch, "E77.28.0.3", {"start": v(280.25, 7) * mm, "mid": v(280, 6.75) * mm, "end": v(279.75, 7) * mm});
            skArc(sketch, "E77.28.0.4", {"start": v(279.75, 19) * mm, "mid": v(280, 19.25) * mm, "end": v(280.25, 19) * mm});
            skLineSegment(sketch, "E77.29.0.0", {"start": v(290.25, 19) * mm, "end": v(290.25, 7) * mm});
            skLineSegment(sketch, "E77.29.0.1", {"start": v(289.75, 19) * mm, "end": v(289.75, 7) * mm});
            skLineSegment(sketch, "E77.29.0.2", {"start": v(290, 19) * mm, "end": v(290, 7) * mm});
            skArc(sketch, "E77.29.0.3", {"start": v(290.25, 7) * mm, "mid": v(290, 6.75) * mm, "end": v(289.75, 7) * mm});
            skArc(sketch, "E77.29.0.4", {"start": v(289.75, 19) * mm, "mid": v(290, 19.25) * mm, "end": v(290.25, 19) * mm});
            skLineSegment(sketch, "E77.30.0.0", {"start": v(300.25, 19) * mm, "end": v(300.25, 7) * mm});
            skLineSegment(sketch, "E77.30.0.1", {"start": v(299.75, 19) * mm, "end": v(299.75, 7) * mm});
            skLineSegment(sketch, "E77.30.0.2", {"start": v(300, 19) * mm, "end": v(300, 7) * mm});
            skArc(sketch, "E77.30.0.3", {"start": v(300.25, 7) * mm, "mid": v(300, 6.75) * mm, "end": v(299.75, 7) * mm});
            skArc(sketch, "E77.30.0.4", {"start": v(299.75, 19) * mm, "mid": v(300, 19.25) * mm, "end": v(300.25, 19) * mm});
            skLineSegment(sketch, "E77.31.0.0", {"start": v(310.25, 19) * mm, "end": v(310.25, 7) * mm});
            skLineSegment(sketch, "E77.31.0.1", {"start": v(309.75, 19) * mm, "end": v(309.75, 7) * mm});
            skLineSegment(sketch, "E77.31.0.2", {"start": v(310, 19) * mm, "end": v(310, 7) * mm});
            skArc(sketch, "E77.31.0.3", {"start": v(310.25, 7) * mm, "mid": v(310, 6.75) * mm, "end": v(309.75, 7) * mm});
            skArc(sketch, "E77.31.0.4", {"start": v(309.75, 19) * mm, "mid": v(310, 19.25) * mm, "end": v(310.25, 19) * mm});
            skLineSegment(sketch, "E77.32.0.0", {"start": v(320.25, 19) * mm, "end": v(320.25, 7) * mm});
            skLineSegment(sketch, "E77.32.0.1", {"start": v(319.75, 19) * mm, "end": v(319.75, 7) * mm});
            skLineSegment(sketch, "E77.32.0.2", {"start": v(320, 19) * mm, "end": v(320, 7) * mm});
            skArc(sketch, "E77.32.0.3", {"start": v(320.25, 7) * mm, "mid": v(320, 6.75) * mm, "end": v(319.75, 7) * mm});
            skArc(sketch, "E77.32.0.4", {"start": v(319.75, 19) * mm, "mid": v(320, 19.25) * mm, "end": v(320.25, 19) * mm});
            skLineSegment(sketch, "E77.33.0.0", {"start": v(330.25, 19) * mm, "end": v(330.25, 7) * mm});
            skLineSegment(sketch, "E77.33.0.1", {"start": v(329.75, 19) * mm, "end": v(329.75, 7) * mm});
            skLineSegment(sketch, "E77.33.0.2", {"start": v(330, 19) * mm, "end": v(330, 7) * mm});
            skArc(sketch, "E77.33.0.3", {"start": v(330.25, 7) * mm, "mid": v(330, 6.75) * mm, "end": v(329.75, 7) * mm});
            skArc(sketch, "E77.33.0.4", {"start": v(329.75, 19) * mm, "mid": v(330, 19.25) * mm, "end": v(330.25, 19) * mm});
            skLineSegment(sketch, "E77.34.0.0", {"start": v(340.25, 19) * mm, "end": v(340.25, 7) * mm});
            skLineSegment(sketch, "E77.34.0.1", {"start": v(339.75, 19) * mm, "end": v(339.75, 7) * mm});
            skLineSegment(sketch, "E77.34.0.2", {"start": v(340, 19) * mm, "end": v(340, 7) * mm});
            skArc(sketch, "E77.34.0.3", {"start": v(340.25, 7) * mm, "mid": v(340, 6.75) * mm, "end": v(339.75, 7) * mm});
            skArc(sketch, "E77.34.0.4", {"start": v(339.75, 19) * mm, "mid": v(340, 19.25) * mm, "end": v(340.25, 19) * mm});
            skLineSegment(sketch, "E77.35.0.0", {"start": v(350.25, 19) * mm, "end": v(350.25, 7) * mm});
            skLineSegment(sketch, "E77.35.0.1", {"start": v(349.75, 19) * mm, "end": v(349.75, 7) * mm});
            skLineSegment(sketch, "E77.35.0.2", {"start": v(350, 19) * mm, "end": v(350, 7) * mm});
            skArc(sketch, "E77.35.0.3", {"start": v(350.25, 7) * mm, "mid": v(350, 6.75) * mm, "end": v(349.75, 7) * mm});
            skArc(sketch, "E77.35.0.4", {"start": v(349.75, 19) * mm, "mid": v(350, 19.25) * mm, "end": v(350.25, 19) * mm});
            skLineSegment(sketch, "E77.36.0.0", {"start": v(360.25, 19) * mm, "end": v(360.25, 7) * mm});
            skLineSegment(sketch, "E77.36.0.1", {"start": v(359.75, 19) * mm, "end": v(359.75, 7) * mm});
            skLineSegment(sketch, "E77.36.0.2", {"start": v(360, 19) * mm, "end": v(360, 7) * mm});
            skArc(sketch, "E77.36.0.3", {"start": v(360.25, 7) * mm, "mid": v(360, 6.75) * mm, "end": v(359.75, 7) * mm});
            skArc(sketch, "E77.36.0.4", {"start": v(359.75, 19) * mm, "mid": v(360, 19.25) * mm, "end": v(360.25, 19) * mm});
            skLineSegment(sketch, "E77.37.0.0", {"start": v(370.25, 19) * mm, "end": v(370.25, 7) * mm});
            skLineSegment(sketch, "E77.37.0.1", {"start": v(369.75, 19) * mm, "end": v(369.75, 7) * mm});
            skLineSegment(sketch, "E77.37.0.2", {"start": v(370, 19) * mm, "end": v(370, 7) * mm});
            skArc(sketch, "E77.37.0.3", {"start": v(370.25, 7) * mm, "mid": v(370, 6.75) * mm, "end": v(369.75, 7) * mm});
            skArc(sketch, "E77.37.0.4", {"start": v(369.75, 19) * mm, "mid": v(370, 19.25) * mm, "end": v(370.25, 19) * mm});
            skLineSegment(sketch, "E77.38.0.0", {"start": v(380.25, 19) * mm, "end": v(380.25, 7) * mm});
            skLineSegment(sketch, "E77.38.0.1", {"start": v(379.75, 19) * mm, "end": v(379.75, 7) * mm});
            skLineSegment(sketch, "E77.38.0.2", {"start": v(380, 19) * mm, "end": v(380, 7) * mm});
            skArc(sketch, "E77.38.0.3", {"start": v(380.25, 7) * mm, "mid": v(380, 6.75) * mm, "end": v(379.75, 7) * mm});
            skArc(sketch, "E77.38.0.4", {"start": v(379.75, 19) * mm, "mid": v(380, 19.25) * mm, "end": v(380.25, 19) * mm});
            skLineSegment(sketch, "E77.39.0.0", {"start": v(390.25, 19) * mm, "end": v(390.25, 7) * mm});
            skLineSegment(sketch, "E77.39.0.1", {"start": v(389.75, 19) * mm, "end": v(389.75, 7) * mm});
            skLineSegment(sketch, "E77.39.0.2", {"start": v(390, 19) * mm, "end": v(390, 7) * mm});
            skArc(sketch, "E77.39.0.3", {"start": v(390.25, 7) * mm, "mid": v(390, 6.75) * mm, "end": v(389.75, 7) * mm});
            skArc(sketch, "E77.39.0.4", {"start": v(389.75, 19) * mm, "mid": v(390, 19.25) * mm, "end": v(390.25, 19) * mm});
            skLineSegment(sketch, "E77.40.0.0", {"start": v(400.25, 19) * mm, "end": v(400.25, 7) * mm});
            skLineSegment(sketch, "E77.40.0.1", {"start": v(399.75, 19) * mm, "end": v(399.75, 7) * mm});
            skLineSegment(sketch, "E77.40.0.2", {"start": v(400, 19) * mm, "end": v(400, 7) * mm});
            skArc(sketch, "E77.40.0.3", {"start": v(400.25, 7) * mm, "mid": v(400, 6.75) * mm, "end": v(399.75, 7) * mm});
            skArc(sketch, "E77.40.0.4", {"start": v(399.75, 19) * mm, "mid": v(400, 19.25) * mm, "end": v(400.25, 19) * mm});
            skLineSegment(sketch, "E77.41.0.0", {"start": v(410.25, 19) * mm, "end": v(410.25, 7) * mm});
            skLineSegment(sketch, "E77.41.0.1", {"start": v(409.75, 19) * mm, "end": v(409.75, 7) * mm});
            skLineSegment(sketch, "E77.41.0.2", {"start": v(410, 19) * mm, "end": v(410, 7) * mm});
            skArc(sketch, "E77.41.0.3", {"start": v(410.25, 7) * mm, "mid": v(410, 6.75) * mm, "end": v(409.75, 7) * mm});
            skArc(sketch, "E77.41.0.4", {"start": v(409.75, 19) * mm, "mid": v(410, 19.25) * mm, "end": v(410.25, 19) * mm});
            skLineSegment(sketch, "E77.42.0.0", {"start": v(420.25, 19) * mm, "end": v(420.25, 7) * mm});
            skLineSegment(sketch, "E77.42.0.1", {"start": v(419.75, 19) * mm, "end": v(419.75, 7) * mm});
            skLineSegment(sketch, "E77.42.0.2", {"start": v(420, 19) * mm, "end": v(420, 7) * mm});
            skArc(sketch, "E77.42.0.3", {"start": v(420.25, 7) * mm, "mid": v(420, 6.75) * mm, "end": v(419.75, 7) * mm});
            skArc(sketch, "E77.42.0.4", {"start": v(419.75, 19) * mm, "mid": v(420, 19.25) * mm, "end": v(420.25, 19) * mm});
            skLineSegment(sketch, "E77.43.0.0", {"start": v(430.25, 19) * mm, "end": v(430.25, 7) * mm});
            skLineSegment(sketch, "E77.43.0.1", {"start": v(429.75, 19) * mm, "end": v(429.75, 7) * mm});
            skLineSegment(sketch, "E77.43.0.2", {"start": v(430, 19) * mm, "end": v(430, 7) * mm});
            skArc(sketch, "E77.43.0.3", {"start": v(430.25, 7) * mm, "mid": v(430, 6.75) * mm, "end": v(429.75, 7) * mm});
            skArc(sketch, "E77.43.0.4", {"start": v(429.75, 19) * mm, "mid": v(430, 19.25) * mm, "end": v(430.25, 19) * mm});
            skLineSegment(sketch, "E77.44.0.0", {"start": v(440.25, 19) * mm, "end": v(440.25, 7) * mm});
            skLineSegment(sketch, "E77.44.0.1", {"start": v(439.75, 19) * mm, "end": v(439.75, 7) * mm});
            skLineSegment(sketch, "E77.44.0.2", {"start": v(440, 19) * mm, "end": v(440, 7) * mm});
            skArc(sketch, "E77.44.0.3", {"start": v(440.25, 7) * mm, "mid": v(440, 6.75) * mm, "end": v(439.75, 7) * mm});
            skArc(sketch, "E77.44.0.4", {"start": v(439.75, 19) * mm, "mid": v(440, 19.25) * mm, "end": v(440.25, 19) * mm});
            skLineSegment(sketch, "E77.45.0.0", {"start": v(450.25, 19) * mm, "end": v(450.25, 7) * mm});
            skLineSegment(sketch, "E77.45.0.1", {"start": v(449.75, 19) * mm, "end": v(449.75, 7) * mm});
            skLineSegment(sketch, "E77.45.0.2", {"start": v(450, 19) * mm, "end": v(450, 7) * mm});
            skArc(sketch, "E77.45.0.3", {"start": v(450.25, 7) * mm, "mid": v(450, 6.75) * mm, "end": v(449.75, 7) * mm});
            skArc(sketch, "E77.45.0.4", {"start": v(449.75, 19) * mm, "mid": v(450, 19.25) * mm, "end": v(450.25, 19) * mm});
            skLineSegment(sketch, "E77.46.0.0", {"start": v(460.25, 19) * mm, "end": v(460.25, 7) * mm});
            skLineSegment(sketch, "E77.46.0.1", {"start": v(459.75, 19) * mm, "end": v(459.75, 7) * mm});
            skLineSegment(sketch, "E77.46.0.2", {"start": v(460, 19) * mm, "end": v(460, 7) * mm});
            skArc(sketch, "E77.46.0.3", {"start": v(460.25, 7) * mm, "mid": v(460, 6.75) * mm, "end": v(459.75, 7) * mm});
            skArc(sketch, "E77.46.0.4", {"start": v(459.75, 19) * mm, "mid": v(460, 19.25) * mm, "end": v(460.25, 19) * mm});
            skLineSegment(sketch, "E77.47.0.0", {"start": v(470.25, 19) * mm, "end": v(470.25, 7) * mm});
            skLineSegment(sketch, "E77.47.0.1", {"start": v(469.75, 19) * mm, "end": v(469.75, 7) * mm});
            skLineSegment(sketch, "E77.47.0.2", {"start": v(470, 19) * mm, "end": v(470, 7) * mm});
            skArc(sketch, "E77.47.0.3", {"start": v(470.25, 7) * mm, "mid": v(470, 6.75) * mm, "end": v(469.75, 7) * mm});
            skArc(sketch, "E77.47.0.4", {"start": v(469.75, 19) * mm, "mid": v(470, 19.25) * mm, "end": v(470.25, 19) * mm});
            skLineSegment(sketch, "E77.48.0.0", {"start": v(480.25, 19) * mm, "end": v(480.25, 7) * mm});
            skLineSegment(sketch, "E77.48.0.1", {"start": v(479.75, 19) * mm, "end": v(479.75, 7) * mm});
            skLineSegment(sketch, "E77.48.0.2", {"start": v(480, 19) * mm, "end": v(480, 7) * mm});
            skArc(sketch, "E77.48.0.3", {"start": v(480.25, 7) * mm, "mid": v(480, 6.75) * mm, "end": v(479.75, 7) * mm});
            skArc(sketch, "E77.48.0.4", {"start": v(479.75, 19) * mm, "mid": v(480, 19.25) * mm, "end": v(480.25, 19) * mm});
            skLineSegment(sketch, "E77.49.0.0", {"start": v(490.25, 19) * mm, "end": v(490.25, 7) * mm});
            skLineSegment(sketch, "E77.49.0.1", {"start": v(489.75, 19) * mm, "end": v(489.75, 7) * mm});
            skLineSegment(sketch, "E77.49.0.2", {"start": v(490, 19) * mm, "end": v(490, 7) * mm});
            skArc(sketch, "E77.49.0.3", {"start": v(490.25, 7) * mm, "mid": v(490, 6.75) * mm, "end": v(489.75, 7) * mm});
            skArc(sketch, "E77.49.0.4", {"start": v(489.75, 19) * mm, "mid": v(490, 19.25) * mm, "end": v(490.25, 19) * mm});
            skLineSegment(sketch, "E77.50.0.0", {"start": v(500.25, 19) * mm, "end": v(500.25, 7) * mm});
            skLineSegment(sketch, "E77.50.0.1", {"start": v(499.75, 19) * mm, "end": v(499.75, 7) * mm});
            skLineSegment(sketch, "E77.50.0.2", {"start": v(500, 19) * mm, "end": v(500, 7) * mm});
            skArc(sketch, "E77.50.0.3", {"start": v(500.25, 7) * mm, "mid": v(500, 6.75) * mm, "end": v(499.75, 7) * mm});
            skArc(sketch, "E77.50.0.4", {"start": v(499.75, 19) * mm, "mid": v(500, 19.25) * mm, "end": v(500.25, 19) * mm});
            skLineSegment(sketch, "E77.51.0.0", {"start": v(510.25, 19) * mm, "end": v(510.25, 7) * mm});
            skLineSegment(sketch, "E77.51.0.1", {"start": v(509.75, 19) * mm, "end": v(509.75, 7) * mm});
            skLineSegment(sketch, "E77.51.0.2", {"start": v(510, 19) * mm, "end": v(510, 7) * mm});
            skArc(sketch, "E77.51.0.3", {"start": v(510.25, 7) * mm, "mid": v(510, 6.75) * mm, "end": v(509.75, 7) * mm});
            skArc(sketch, "E77.51.0.4", {"start": v(509.75, 19) * mm, "mid": v(510, 19.25) * mm, "end": v(510.25, 19) * mm});
            skLineSegment(sketch, "E77.52.0.0", {"start": v(520.25, 19) * mm, "end": v(520.25, 7) * mm});
            skLineSegment(sketch, "E77.52.0.1", {"start": v(519.75, 19) * mm, "end": v(519.75, 7) * mm});
            skLineSegment(sketch, "E77.52.0.2", {"start": v(520, 19) * mm, "end": v(520, 7) * mm});
            skArc(sketch, "E77.52.0.3", {"start": v(520.25, 7) * mm, "mid": v(520, 6.75) * mm, "end": v(519.75, 7) * mm});
            skArc(sketch, "E77.52.0.4", {"start": v(519.75, 19) * mm, "mid": v(520, 19.25) * mm, "end": v(520.25, 19) * mm});
            skLineSegment(sketch, "E77.53.0.0", {"start": v(530.25, 19) * mm, "end": v(530.25, 7) * mm});
            skLineSegment(sketch, "E77.53.0.1", {"start": v(529.75, 19) * mm, "end": v(529.75, 7) * mm});
            skLineSegment(sketch, "E77.53.0.2", {"start": v(530, 19) * mm, "end": v(530, 7) * mm});
            skArc(sketch, "E77.53.0.3", {"start": v(530.25, 7) * mm, "mid": v(530, 6.75) * mm, "end": v(529.75, 7) * mm});
            skArc(sketch, "E77.53.0.4", {"start": v(529.75, 19) * mm, "mid": v(530, 19.25) * mm, "end": v(530.25, 19) * mm});
            skLineSegment(sketch, "E77.54.0.0", {"start": v(540.25, 19) * mm, "end": v(540.25, 7) * mm});
            skLineSegment(sketch, "E77.54.0.1", {"start": v(539.75, 19) * mm, "end": v(539.75, 7) * mm});
            skLineSegment(sketch, "E77.54.0.2", {"start": v(540, 19) * mm, "end": v(540, 7) * mm});
            skArc(sketch, "E77.54.0.3", {"start": v(540.25, 7) * mm, "mid": v(540, 6.75) * mm, "end": v(539.75, 7) * mm});
            skArc(sketch, "E77.54.0.4", {"start": v(539.75, 19) * mm, "mid": v(540, 19.25) * mm, "end": v(540.25, 19) * mm});
            skLineSegment(sketch, "E77.55.0.0", {"start": v(550.25, 19) * mm, "end": v(550.25, 7) * mm});
            skLineSegment(sketch, "E77.55.0.1", {"start": v(549.75, 19) * mm, "end": v(549.75, 7) * mm});
            skLineSegment(sketch, "E77.55.0.2", {"start": v(550, 19) * mm, "end": v(550, 7) * mm});
            skArc(sketch, "E77.55.0.3", {"start": v(550.25, 7) * mm, "mid": v(550, 6.75) * mm, "end": v(549.75, 7) * mm});
            skArc(sketch, "E77.55.0.4", {"start": v(549.75, 19) * mm, "mid": v(550, 19.25) * mm, "end": v(550.25, 19) * mm});
            skLineSegment(sketch, "E77.56.0.0", {"start": v(560.25, 19) * mm, "end": v(560.25, 7) * mm});
            skLineSegment(sketch, "E77.56.0.1", {"start": v(559.75, 19) * mm, "end": v(559.75, 7) * mm});
            skLineSegment(sketch, "E77.56.0.2", {"start": v(560, 19) * mm, "end": v(560, 7) * mm});
            skArc(sketch, "E77.56.0.3", {"start": v(560.25, 7) * mm, "mid": v(560, 6.75) * mm, "end": v(559.75, 7) * mm});
            skArc(sketch, "E77.56.0.4", {"start": v(559.75, 19) * mm, "mid": v(560, 19.25) * mm, "end": v(560.25, 19) * mm});
            skLineSegment(sketch, "E77.57.0.0", {"start": v(570.25, 19) * mm, "end": v(570.25, 7) * mm});
            skLineSegment(sketch, "E77.57.0.1", {"start": v(569.75, 19) * mm, "end": v(569.75, 7) * mm});
            skLineSegment(sketch, "E77.57.0.2", {"start": v(570, 19) * mm, "end": v(570, 7) * mm});
            skArc(sketch, "E77.57.0.3", {"start": v(570.25, 7) * mm, "mid": v(570, 6.75) * mm, "end": v(569.75, 7) * mm});
            skArc(sketch, "E77.57.0.4", {"start": v(569.75, 19) * mm, "mid": v(570, 19.25) * mm, "end": v(570.25, 19) * mm});
            skLineSegment(sketch, "E77.58.0.0", {"start": v(580.25, 19) * mm, "end": v(580.25, 7) * mm});
            skLineSegment(sketch, "E77.58.0.1", {"start": v(579.75, 19) * mm, "end": v(579.75, 7) * mm});
            skLineSegment(sketch, "E77.58.0.2", {"start": v(580, 19) * mm, "end": v(580, 7) * mm});
            skArc(sketch, "E77.58.0.3", {"start": v(580.25, 7) * mm, "mid": v(580, 6.75) * mm, "end": v(579.75, 7) * mm});
            skArc(sketch, "E77.58.0.4", {"start": v(579.75, 19) * mm, "mid": v(580, 19.25) * mm, "end": v(580.25, 19) * mm});
            skLineSegment(sketch, "E77.59.0.0", {"start": v(590.25, 19) * mm, "end": v(590.25, 7) * mm});
            skLineSegment(sketch, "E77.59.0.1", {"start": v(589.75, 19) * mm, "end": v(589.75, 7) * mm});
            skLineSegment(sketch, "E77.59.0.2", {"start": v(590, 19) * mm, "end": v(590, 7) * mm});
            skArc(sketch, "E77.59.0.3", {"start": v(590.25, 7) * mm, "mid": v(590, 6.75) * mm, "end": v(589.75, 7) * mm});
            skArc(sketch, "E77.59.0.4", {"start": v(589.75, 19) * mm, "mid": v(590, 19.25) * mm, "end": v(590.25, 19) * mm});
            skLineSegment(sketch, "E77.60.0.0", {"start": v(600.25, 19) * mm, "end": v(600.25, 7) * mm});
            skLineSegment(sketch, "E77.60.0.1", {"start": v(599.75, 19) * mm, "end": v(599.75, 7) * mm});
            skLineSegment(sketch, "E77.60.0.2", {"start": v(600, 19) * mm, "end": v(600, 7) * mm});
            skArc(sketch, "E77.60.0.3", {"start": v(600.25, 7) * mm, "mid": v(600, 6.75) * mm, "end": v(599.75, 7) * mm});
            skArc(sketch, "E77.60.0.4", {"start": v(599.75, 19) * mm, "mid": v(600, 19.25) * mm, "end": v(600.25, 19) * mm});
            skLineSegment(sketch, "E77.61.0.0", {"start": v(610.25, 19) * mm, "end": v(610.25, 7) * mm});
            skLineSegment(sketch, "E77.61.0.1", {"start": v(609.75, 19) * mm, "end": v(609.75, 7) * mm});
            skLineSegment(sketch, "E77.61.0.2", {"start": v(610, 19) * mm, "end": v(610, 7) * mm});
            skArc(sketch, "E77.61.0.3", {"start": v(610.25, 7) * mm, "mid": v(610, 6.75) * mm, "end": v(609.75, 7) * mm});
            skArc(sketch, "E77.61.0.4", {"start": v(609.75, 19) * mm, "mid": v(610, 19.25) * mm, "end": v(610.25, 19) * mm});
            skLineSegment(sketch, "E77.62.0.0", {"start": v(620.25, 19) * mm, "end": v(620.25, 7) * mm});
            skLineSegment(sketch, "E77.62.0.1", {"start": v(619.75, 19) * mm, "end": v(619.75, 7) * mm});
            skLineSegment(sketch, "E77.62.0.2", {"start": v(620, 19) * mm, "end": v(620, 7) * mm});
            skArc(sketch, "E77.62.0.3", {"start": v(620.25, 7) * mm, "mid": v(620, 6.75) * mm, "end": v(619.75, 7) * mm});
            skArc(sketch, "E77.62.0.4", {"start": v(619.75, 19) * mm, "mid": v(620, 19.25) * mm, "end": v(620.25, 19) * mm});
            skLineSegment(sketch, "E77.63.0.0", {"start": v(630.25, 19) * mm, "end": v(630.25, 7) * mm});
            skLineSegment(sketch, "E77.63.0.1", {"start": v(629.75, 19) * mm, "end": v(629.75, 7) * mm});
            skLineSegment(sketch, "E77.63.0.2", {"start": v(630, 19) * mm, "end": v(630, 7) * mm});
            skArc(sketch, "E77.63.0.3", {"start": v(630.25, 7) * mm, "mid": v(630, 6.75) * mm, "end": v(629.75, 7) * mm});
            skArc(sketch, "E77.63.0.4", {"start": v(629.75, 19) * mm, "mid": v(630, 19.25) * mm, "end": v(630.25, 19) * mm});
            skLineSegment(sketch, "E77.64.0.0", {"start": v(640.25, 19) * mm, "end": v(640.25, 7) * mm});
            skLineSegment(sketch, "E77.64.0.1", {"start": v(639.75, 19) * mm, "end": v(639.75, 7) * mm});
            skLineSegment(sketch, "E77.64.0.2", {"start": v(640, 19) * mm, "end": v(640, 7) * mm});
            skArc(sketch, "E77.64.0.3", {"start": v(640.25, 7) * mm, "mid": v(640, 6.75) * mm, "end": v(639.75, 7) * mm});
            skArc(sketch, "E77.64.0.4", {"start": v(639.75, 19) * mm, "mid": v(640, 19.25) * mm, "end": v(640.25, 19) * mm});
            skLineSegment(sketch, "E77.65.0.0", {"start": v(650.25, 19) * mm, "end": v(650.25, 7) * mm});
            skLineSegment(sketch, "E77.65.0.1", {"start": v(649.75, 19) * mm, "end": v(649.75, 7) * mm});
            skLineSegment(sketch, "E77.65.0.2", {"start": v(650, 19) * mm, "end": v(650, 7) * mm});
            skArc(sketch, "E77.65.0.3", {"start": v(650.25, 7) * mm, "mid": v(650, 6.75) * mm, "end": v(649.75, 7) * mm});
            skArc(sketch, "E77.65.0.4", {"start": v(649.75, 19) * mm, "mid": v(650, 19.25) * mm, "end": v(650.25, 19) * mm});
            skLineSegment(sketch, "E77.66.0.0", {"start": v(660.25, 19) * mm, "end": v(660.25, 7) * mm});
            skLineSegment(sketch, "E77.66.0.1", {"start": v(659.75, 19) * mm, "end": v(659.75, 7) * mm});
            skLineSegment(sketch, "E77.66.0.2", {"start": v(660, 19) * mm, "end": v(660, 7) * mm});
            skArc(sketch, "E77.66.0.3", {"start": v(660.25, 7) * mm, "mid": v(660, 6.75) * mm, "end": v(659.75, 7) * mm});
            skArc(sketch, "E77.66.0.4", {"start": v(659.75, 19) * mm, "mid": v(660, 19.25) * mm, "end": v(660.25, 19) * mm});
            skLineSegment(sketch, "E77.67.0.0", {"start": v(670.25, 19) * mm, "end": v(670.25, 7) * mm});
            skLineSegment(sketch, "E77.67.0.1", {"start": v(669.75, 19) * mm, "end": v(669.75, 7) * mm});
            skLineSegment(sketch, "E77.67.0.2", {"start": v(670, 19) * mm, "end": v(670, 7) * mm});
            skArc(sketch, "E77.67.0.3", {"start": v(670.25, 7) * mm, "mid": v(670, 6.75) * mm, "end": v(669.75, 7) * mm});
            skArc(sketch, "E77.67.0.4", {"start": v(669.75, 19) * mm, "mid": v(670, 19.25) * mm, "end": v(670.25, 19) * mm});
            skLineSegment(sketch, "E77.68.0.0", {"start": v(680.25, 19) * mm, "end": v(680.25, 7) * mm});
            skLineSegment(sketch, "E77.68.0.1", {"start": v(679.75, 19) * mm, "end": v(679.75, 7) * mm});
            skLineSegment(sketch, "E77.68.0.2", {"start": v(680, 19) * mm, "end": v(680, 7) * mm});
            skArc(sketch, "E77.68.0.3", {"start": v(680.25, 7) * mm, "mid": v(680, 6.75) * mm, "end": v(679.75, 7) * mm});
            skArc(sketch, "E77.68.0.4", {"start": v(679.75, 19) * mm, "mid": v(680, 19.25) * mm, "end": v(680.25, 19) * mm});
            skLineSegment(sketch, "E77.69.0.0", {"start": v(690.25, 19) * mm, "end": v(690.25, 7) * mm});
            skLineSegment(sketch, "E77.69.0.1", {"start": v(689.75, 19) * mm, "end": v(689.75, 7) * mm});
            skLineSegment(sketch, "E77.69.0.2", {"start": v(690, 19) * mm, "end": v(690, 7) * mm});
            skArc(sketch, "E77.69.0.3", {"start": v(690.25, 7) * mm, "mid": v(690, 6.75) * mm, "end": v(689.75, 7) * mm});
            skArc(sketch, "E77.69.0.4", {"start": v(689.75, 19) * mm, "mid": v(690, 19.25) * mm, "end": v(690.25, 19) * mm});
            skLineSegment(sketch, "E77.70.0.0", {"start": v(700.25, 19) * mm, "end": v(700.25, 7) * mm});
            skLineSegment(sketch, "E77.70.0.1", {"start": v(699.75, 19) * mm, "end": v(699.75, 7) * mm});
            skLineSegment(sketch, "E77.70.0.2", {"start": v(700, 19) * mm, "end": v(700, 7) * mm});
            skArc(sketch, "E77.70.0.3", {"start": v(700.25, 7) * mm, "mid": v(700, 6.75) * mm, "end": v(699.75, 7) * mm});
            skArc(sketch, "E77.70.0.4", {"start": v(699.75, 19) * mm, "mid": v(700, 19.25) * mm, "end": v(700.25, 19) * mm});
            skLineSegment(sketch, "E77.71.0.0", {"start": v(710.25, 19) * mm, "end": v(710.25, 7) * mm});
            skLineSegment(sketch, "E77.71.0.1", {"start": v(709.75, 19) * mm, "end": v(709.75, 7) * mm});
            skLineSegment(sketch, "E77.71.0.2", {"start": v(710, 19) * mm, "end": v(710, 7) * mm});
            skArc(sketch, "E77.71.0.3", {"start": v(710.25, 7) * mm, "mid": v(710, 6.75) * mm, "end": v(709.75, 7) * mm});
            skArc(sketch, "E77.71.0.4", {"start": v(709.75, 19) * mm, "mid": v(710, 19.25) * mm, "end": v(710.25, 19) * mm});
            skLineSegment(sketch, "E77.72.0.0", {"start": v(720.25, 19) * mm, "end": v(720.25, 7) * mm});
            skLineSegment(sketch, "E77.72.0.1", {"start": v(719.75, 19) * mm, "end": v(719.75, 7) * mm});
            skLineSegment(sketch, "E77.72.0.2", {"start": v(720, 19) * mm, "end": v(720, 7) * mm});
            skArc(sketch, "E77.72.0.3", {"start": v(720.25, 7) * mm, "mid": v(720, 6.75) * mm, "end": v(719.75, 7) * mm});
            skArc(sketch, "E77.72.0.4", {"start": v(719.75, 19) * mm, "mid": v(720, 19.25) * mm, "end": v(720.25, 19) * mm});
            skLineSegment(sketch, "E77.73.0.0", {"start": v(730.25, 19) * mm, "end": v(730.25, 7) * mm});
            skLineSegment(sketch, "E77.73.0.1", {"start": v(729.75, 19) * mm, "end": v(729.75, 7) * mm});
            skLineSegment(sketch, "E77.73.0.2", {"start": v(730, 19) * mm, "end": v(730, 7) * mm});
            skArc(sketch, "E77.73.0.3", {"start": v(730.25, 7) * mm, "mid": v(730, 6.75) * mm, "end": v(729.75, 7) * mm});
            skArc(sketch, "E77.73.0.4", {"start": v(729.75, 19) * mm, "mid": v(730, 19.25) * mm, "end": v(730.25, 19) * mm});
            skLineSegment(sketch, "E77.74.0.0", {"start": v(740.25, 19) * mm, "end": v(740.25, 7) * mm});
            skLineSegment(sketch, "E77.74.0.1", {"start": v(739.75, 19) * mm, "end": v(739.75, 7) * mm});
            skLineSegment(sketch, "E77.74.0.2", {"start": v(740, 19) * mm, "end": v(740, 7) * mm});
            skArc(sketch, "E77.74.0.3", {"start": v(740.25, 7) * mm, "mid": v(740, 6.75) * mm, "end": v(739.75, 7) * mm});
            skArc(sketch, "E77.74.0.4", {"start": v(739.75, 19) * mm, "mid": v(740, 19.25) * mm, "end": v(740.25, 19) * mm});
            skLineSegment(sketch, "E77.75.0.0", {"start": v(750.25, 19) * mm, "end": v(750.25, 7) * mm});
            skLineSegment(sketch, "E77.75.0.1", {"start": v(749.75, 19) * mm, "end": v(749.75, 7) * mm});
            skLineSegment(sketch, "E77.75.0.2", {"start": v(750, 19) * mm, "end": v(750, 7) * mm});
            skArc(sketch, "E77.75.0.3", {"start": v(750.25, 7) * mm, "mid": v(750, 6.75) * mm, "end": v(749.75, 7) * mm});
            skArc(sketch, "E77.75.0.4", {"start": v(749.75, 19) * mm, "mid": v(750, 19.25) * mm, "end": v(750.25, 19) * mm});
            skLineSegment(sketch, "E77.76.0.0", {"start": v(760.25, 19) * mm, "end": v(760.25, 7) * mm});
            skLineSegment(sketch, "E77.76.0.1", {"start": v(759.75, 19) * mm, "end": v(759.75, 7) * mm});
            skLineSegment(sketch, "E77.76.0.2", {"start": v(760, 19) * mm, "end": v(760, 7) * mm});
            skArc(sketch, "E77.76.0.3", {"start": v(760.25, 7) * mm, "mid": v(760, 6.75) * mm, "end": v(759.75, 7) * mm});
            skArc(sketch, "E77.76.0.4", {"start": v(759.75, 19) * mm, "mid": v(760, 19.25) * mm, "end": v(760.25, 19) * mm});
            skLineSegment(sketch, "E77.77.0.0", {"start": v(770.25, 19) * mm, "end": v(770.25, 7) * mm});
            skLineSegment(sketch, "E77.77.0.1", {"start": v(769.75, 19) * mm, "end": v(769.75, 7) * mm});
            skLineSegment(sketch, "E77.77.0.2", {"start": v(770, 19) * mm, "end": v(770, 7) * mm});
            skArc(sketch, "E77.77.0.3", {"start": v(770.25, 7) * mm, "mid": v(770, 6.75) * mm, "end": v(769.75, 7) * mm});
            skArc(sketch, "E77.77.0.4", {"start": v(769.75, 19) * mm, "mid": v(770, 19.25) * mm, "end": v(770.25, 19) * mm});
            skLineSegment(sketch, "E77.78.0.0", {"start": v(780.25, 19) * mm, "end": v(780.25, 7) * mm});
            skLineSegment(sketch, "E77.78.0.1", {"start": v(779.75, 19) * mm, "end": v(779.75, 7) * mm});
            skLineSegment(sketch, "E77.78.0.2", {"start": v(780, 19) * mm, "end": v(780, 7) * mm});
            skArc(sketch, "E77.78.0.3", {"start": v(780.25, 7) * mm, "mid": v(780, 6.75) * mm, "end": v(779.75, 7) * mm});
            skArc(sketch, "E77.78.0.4", {"start": v(779.75, 19) * mm, "mid": v(780, 19.25) * mm, "end": v(780.25, 19) * mm});
            skLineSegment(sketch, "E77.79.0.0", {"start": v(790.25, 19) * mm, "end": v(790.25, 7) * mm});
            skLineSegment(sketch, "E77.79.0.1", {"start": v(789.75, 19) * mm, "end": v(789.75, 7) * mm});
            skLineSegment(sketch, "E77.79.0.2", {"start": v(790, 19) * mm, "end": v(790, 7) * mm});
            skArc(sketch, "E77.79.0.3", {"start": v(790.25, 7) * mm, "mid": v(790, 6.75) * mm, "end": v(789.75, 7) * mm});
            skArc(sketch, "E77.79.0.4", {"start": v(789.75, 19) * mm, "mid": v(790, 19.25) * mm, "end": v(790.25, 19) * mm});
            skLineSegment(sketch, "E77.80.0.0", {"start": v(800.25, 19) * mm, "end": v(800.25, 7) * mm});
            skLineSegment(sketch, "E77.80.0.1", {"start": v(799.75, 19) * mm, "end": v(799.75, 7) * mm});
            skLineSegment(sketch, "E77.80.0.2", {"start": v(800, 19) * mm, "end": v(800, 7) * mm});
            skArc(sketch, "E77.80.0.3", {"start": v(800.25, 7) * mm, "mid": v(800, 6.75) * mm, "end": v(799.75, 7) * mm});
            skArc(sketch, "E77.80.0.4", {"start": v(799.75, 19) * mm, "mid": v(800, 19.25) * mm, "end": v(800.25, 19) * mm});
            skLineSegment(sketch, "E77.81.0.0", {"start": v(810.25, 19) * mm, "end": v(810.25, 7) * mm});
            skLineSegment(sketch, "E77.81.0.1", {"start": v(809.75, 19) * mm, "end": v(809.75, 7) * mm});
            skLineSegment(sketch, "E77.81.0.2", {"start": v(810, 19) * mm, "end": v(810, 7) * mm});
            skArc(sketch, "E77.81.0.3", {"start": v(810.25, 7) * mm, "mid": v(810, 6.75) * mm, "end": v(809.75, 7) * mm});
            skArc(sketch, "E77.81.0.4", {"start": v(809.75, 19) * mm, "mid": v(810, 19.25) * mm, "end": v(810.25, 19) * mm});
            skLineSegment(sketch, "E77.82.0.0", {"start": v(820.25, 19) * mm, "end": v(820.25, 7) * mm});
            skLineSegment(sketch, "E77.82.0.1", {"start": v(819.75, 19) * mm, "end": v(819.75, 7) * mm});
            skLineSegment(sketch, "E77.82.0.2", {"start": v(820, 19) * mm, "end": v(820, 7) * mm});
            skArc(sketch, "E77.82.0.3", {"start": v(820.25, 7) * mm, "mid": v(820, 6.75) * mm, "end": v(819.75, 7) * mm});
            skArc(sketch, "E77.82.0.4", {"start": v(819.75, 19) * mm, "mid": v(820, 19.25) * mm, "end": v(820.25, 19) * mm});
            skLineSegment(sketch, "E77.83.0.0", {"start": v(830.25, 19) * mm, "end": v(830.25, 7) * mm});
            skLineSegment(sketch, "E77.83.0.1", {"start": v(829.75, 19) * mm, "end": v(829.75, 7) * mm});
            skLineSegment(sketch, "E77.83.0.2", {"start": v(830, 19) * mm, "end": v(830, 7) * mm});
            skArc(sketch, "E77.83.0.3", {"start": v(830.25, 7) * mm, "mid": v(830, 6.75) * mm, "end": v(829.75, 7) * mm});
            skArc(sketch, "E77.83.0.4", {"start": v(829.75, 19) * mm, "mid": v(830, 19.25) * mm, "end": v(830.25, 19) * mm});
            skLineSegment(sketch, "E77.84.0.0", {"start": v(840.25, 19) * mm, "end": v(840.25, 7) * mm});
            skLineSegment(sketch, "E77.84.0.1", {"start": v(839.75, 19) * mm, "end": v(839.75, 7) * mm});
            skLineSegment(sketch, "E77.84.0.2", {"start": v(840, 19) * mm, "end": v(840, 7) * mm});
            skArc(sketch, "E77.84.0.3", {"start": v(840.25, 7) * mm, "mid": v(840, 6.75) * mm, "end": v(839.75, 7) * mm});
            skArc(sketch, "E77.84.0.4", {"start": v(839.75, 19) * mm, "mid": v(840, 19.25) * mm, "end": v(840.25, 19) * mm});
            skLineSegment(sketch, "E77.85.0.0", {"start": v(850.25, 19) * mm, "end": v(850.25, 7) * mm});
            skLineSegment(sketch, "E77.85.0.1", {"start": v(849.75, 19) * mm, "end": v(849.75, 7) * mm});
            skLineSegment(sketch, "E77.85.0.2", {"start": v(850, 19) * mm, "end": v(850, 7) * mm});
            skArc(sketch, "E77.85.0.3", {"start": v(850.25, 7) * mm, "mid": v(850, 6.75) * mm, "end": v(849.75, 7) * mm});
            skArc(sketch, "E77.85.0.4", {"start": v(849.75, 19) * mm, "mid": v(850, 19.25) * mm, "end": v(850.25, 19) * mm});
            skLineSegment(sketch, "E77.86.0.0", {"start": v(860.25, 19) * mm, "end": v(860.25, 7) * mm});
            skLineSegment(sketch, "E77.86.0.1", {"start": v(859.75, 19) * mm, "end": v(859.75, 7) * mm});
            skLineSegment(sketch, "E77.86.0.2", {"start": v(860, 19) * mm, "end": v(860, 7) * mm});
            skArc(sketch, "E77.86.0.3", {"start": v(860.25, 7) * mm, "mid": v(860, 6.75) * mm, "end": v(859.75, 7) * mm});
            skArc(sketch, "E77.86.0.4", {"start": v(859.75, 19) * mm, "mid": v(860, 19.25) * mm, "end": v(860.25, 19) * mm});
            skLineSegment(sketch, "E77.87.0.0", {"start": v(870.25, 19) * mm, "end": v(870.25, 7) * mm});
            skLineSegment(sketch, "E77.87.0.1", {"start": v(869.75, 19) * mm, "end": v(869.75, 7) * mm});
            skLineSegment(sketch, "E77.87.0.2", {"start": v(870, 19) * mm, "end": v(870, 7) * mm});
            skArc(sketch, "E77.87.0.3", {"start": v(870.25, 7) * mm, "mid": v(870, 6.75) * mm, "end": v(869.75, 7) * mm});
            skArc(sketch, "E77.87.0.4", {"start": v(869.75, 19) * mm, "mid": v(870, 19.25) * mm, "end": v(870.25, 19) * mm});
            skLineSegment(sketch, "E77.88.0.0", {"start": v(880.25, 19) * mm, "end": v(880.25, 7) * mm});
            skLineSegment(sketch, "E77.88.0.1", {"start": v(879.75, 19) * mm, "end": v(879.75, 7) * mm});
            skLineSegment(sketch, "E77.88.0.2", {"start": v(880, 19) * mm, "end": v(880, 7) * mm});
            skArc(sketch, "E77.88.0.3", {"start": v(880.25, 7) * mm, "mid": v(880, 6.75) * mm, "end": v(879.75, 7) * mm});
            skArc(sketch, "E77.88.0.4", {"start": v(879.75, 19) * mm, "mid": v(880, 19.25) * mm, "end": v(880.25, 19) * mm});
            skLineSegment(sketch, "E77.89.0.0", {"start": v(890.25, 19) * mm, "end": v(890.25, 7) * mm});
            skLineSegment(sketch, "E77.89.0.1", {"start": v(889.75, 19) * mm, "end": v(889.75, 7) * mm});
            skLineSegment(sketch, "E77.89.0.2", {"start": v(890, 19) * mm, "end": v(890, 7) * mm});
            skArc(sketch, "E77.89.0.3", {"start": v(890.25, 7) * mm, "mid": v(890, 6.75) * mm, "end": v(889.75, 7) * mm});
            skArc(sketch, "E77.89.0.4", {"start": v(889.75, 19) * mm, "mid": v(890, 19.25) * mm, "end": v(890.25, 19) * mm});
            skLineSegment(sketch, "E77.90.0.0", {"start": v(900.25, 19) * mm, "end": v(900.25, 7) * mm});
            skLineSegment(sketch, "E77.90.0.1", {"start": v(899.75, 19) * mm, "end": v(899.75, 7) * mm});
            skLineSegment(sketch, "E77.90.0.2", {"start": v(900, 19) * mm, "end": v(900, 7) * mm});
            skArc(sketch, "E77.90.0.3", {"start": v(900.25, 7) * mm, "mid": v(900, 6.75) * mm, "end": v(899.75, 7) * mm});
            skArc(sketch, "E77.90.0.4", {"start": v(899.75, 19) * mm, "mid": v(900, 19.25) * mm, "end": v(900.25, 19) * mm});
            skLineSegment(sketch, "E77.91.0.0", {"start": v(910.25, 19) * mm, "end": v(910.25, 7) * mm});
            skLineSegment(sketch, "E77.91.0.1", {"start": v(909.75, 19) * mm, "end": v(909.75, 7) * mm});
            skLineSegment(sketch, "E77.91.0.2", {"start": v(910, 19) * mm, "end": v(910, 7) * mm});
            skArc(sketch, "E77.91.0.3", {"start": v(910.25, 7) * mm, "mid": v(910, 6.75) * mm, "end": v(909.75, 7) * mm});
            skArc(sketch, "E77.91.0.4", {"start": v(909.75, 19) * mm, "mid": v(910, 19.25) * mm, "end": v(910.25, 19) * mm});
            skLineSegment(sketch, "E77.92.0.0", {"start": v(920.25, 19) * mm, "end": v(920.25, 7) * mm});
            skLineSegment(sketch, "E77.92.0.1", {"start": v(919.75, 19) * mm, "end": v(919.75, 7) * mm});
            skLineSegment(sketch, "E77.92.0.2", {"start": v(920, 19) * mm, "end": v(920, 7) * mm});
            skArc(sketch, "E77.92.0.3", {"start": v(920.25, 7) * mm, "mid": v(920, 6.75) * mm, "end": v(919.75, 7) * mm});
            skArc(sketch, "E77.92.0.4", {"start": v(919.75, 19) * mm, "mid": v(920, 19.25) * mm, "end": v(920.25, 19) * mm});
            skLineSegment(sketch, "E77.93.0.0", {"start": v(930.25, 19) * mm, "end": v(930.25, 7) * mm});
            skLineSegment(sketch, "E77.93.0.1", {"start": v(929.75, 19) * mm, "end": v(929.75, 7) * mm});
            skLineSegment(sketch, "E77.93.0.2", {"start": v(930, 19) * mm, "end": v(930, 7) * mm});
            skArc(sketch, "E77.93.0.3", {"start": v(930.25, 7) * mm, "mid": v(930, 6.75) * mm, "end": v(929.75, 7) * mm});
            skArc(sketch, "E77.93.0.4", {"start": v(929.75, 19) * mm, "mid": v(930, 19.25) * mm, "end": v(930.25, 19) * mm});
            skLineSegment(sketch, "E77.94.0.0", {"start": v(940.25, 19) * mm, "end": v(940.25, 7) * mm});
            skLineSegment(sketch, "E77.94.0.1", {"start": v(939.75, 19) * mm, "end": v(939.75, 7) * mm});
            skLineSegment(sketch, "E77.94.0.2", {"start": v(940, 19) * mm, "end": v(940, 7) * mm});
            skArc(sketch, "E77.94.0.3", {"start": v(940.25, 7) * mm, "mid": v(940, 6.75) * mm, "end": v(939.75, 7) * mm});
            skArc(sketch, "E77.94.0.4", {"start": v(939.75, 19) * mm, "mid": v(940, 19.25) * mm, "end": v(940.25, 19) * mm});
            skLineSegment(sketch, "E77.95.0.0", {"start": v(950.25, 19) * mm, "end": v(950.25, 7) * mm});
            skLineSegment(sketch, "E77.95.0.1", {"start": v(949.75, 19) * mm, "end": v(949.75, 7) * mm});
            skLineSegment(sketch, "E77.95.0.2", {"start": v(950, 19) * mm, "end": v(950, 7) * mm});
            skArc(sketch, "E77.95.0.3", {"start": v(950.25, 7) * mm, "mid": v(950, 6.75) * mm, "end": v(949.75, 7) * mm});
            skArc(sketch, "E77.95.0.4", {"start": v(949.75, 19) * mm, "mid": v(950, 19.25) * mm, "end": v(950.25, 19) * mm});
            skLineSegment(sketch, "E77.96.0.0", {"start": v(960.25, 19) * mm, "end": v(960.25, 7) * mm});
            skLineSegment(sketch, "E77.96.0.1", {"start": v(959.75, 19) * mm, "end": v(959.75, 7) * mm});
            skLineSegment(sketch, "E77.96.0.2", {"start": v(960, 19) * mm, "end": v(960, 7) * mm});
            skArc(sketch, "E77.96.0.3", {"start": v(960.25, 7) * mm, "mid": v(960, 6.75) * mm, "end": v(959.75, 7) * mm});
            skArc(sketch, "E77.96.0.4", {"start": v(959.75, 19) * mm, "mid": v(960, 19.25) * mm, "end": v(960.25, 19) * mm});
            skLineSegment(sketch, "E77.97.0.0", {"start": v(970.25, 19) * mm, "end": v(970.25, 7) * mm});
            skLineSegment(sketch, "E77.97.0.1", {"start": v(969.75, 19) * mm, "end": v(969.75, 7) * mm});
            skLineSegment(sketch, "E77.97.0.2", {"start": v(970, 19) * mm, "end": v(970, 7) * mm});
            skArc(sketch, "E77.97.0.3", {"start": v(970.25, 7) * mm, "mid": v(970, 6.75) * mm, "end": v(969.75, 7) * mm});
            skArc(sketch, "E77.97.0.4", {"start": v(969.75, 19) * mm, "mid": v(970, 19.25) * mm, "end": v(970.25, 19) * mm});
            skLineSegment(sketch, "E77.98.0.0", {"start": v(980.25, 19) * mm, "end": v(980.25, 7) * mm});
            skLineSegment(sketch, "E77.98.0.1", {"start": v(979.75, 19) * mm, "end": v(979.75, 7) * mm});
            skLineSegment(sketch, "E77.98.0.2", {"start": v(980, 19) * mm, "end": v(980, 7) * mm});
            skArc(sketch, "E77.98.0.3", {"start": v(980.25, 7) * mm, "mid": v(980, 6.75) * mm, "end": v(979.75, 7) * mm});
            skArc(sketch, "E77.98.0.4", {"start": v(979.75, 19) * mm, "mid": v(980, 19.25) * mm, "end": v(980.25, 19) * mm});
            skLineSegment(sketch, "E77.99.0.0", {"start": v(990.25, 19) * mm, "end": v(990.25, 7) * mm});
            skLineSegment(sketch, "E77.99.0.1", {"start": v(989.75, 19) * mm, "end": v(989.75, 7) * mm});
            skLineSegment(sketch, "E77.99.0.2", {"start": v(990, 19) * mm, "end": v(990, 7) * mm});
            skArc(sketch, "E77.99.0.3", {"start": v(990.25, 7) * mm, "mid": v(990, 6.75) * mm, "end": v(989.75, 7) * mm});
            skArc(sketch, "E77.99.0.4", {"start": v(989.75, 19) * mm, "mid": v(990, 19.25) * mm, "end": v(990.25, 19) * mm});
            skLineSegment(sketch, "E77.direction1", {"start": v(-0.25, 7) * mm, "end": v(9.75, 7) * mm, "construction": true});
            skLineSegment(sketch, "E78.1.0.0", {"start": v(1000.25, 19) * mm, "end": v(1000.25, 7) * mm});
            skLineSegment(sketch, "E78.1.0.1", {"start": v(999.75, 19) * mm, "end": v(999.75, 7) * mm});
            skLineSegment(sketch, "E78.1.0.2", {"start": v(1000, 19) * mm, "end": v(1000, 7) * mm});
            skArc(sketch, "E78.1.0.3", {"start": v(999.75, 19) * mm, "mid": v(1000, 19.25) * mm, "end": v(1000.25, 19) * mm});
            skArc(sketch, "E78.1.0.4", {"start": v(1000.25, 7) * mm, "mid": v(1000, 6.75) * mm, "end": v(999.75, 7) * mm});
            skLineSegment(sketch, "E78.2.0.0", {"start": v(1010.25, 19) * mm, "end": v(1010.25, 7) * mm});
            skLineSegment(sketch, "E78.2.0.1", {"start": v(1009.75, 19) * mm, "end": v(1009.75, 7) * mm});
            skLineSegment(sketch, "E78.2.0.2", {"start": v(1010, 19) * mm, "end": v(1010, 7) * mm});
            skArc(sketch, "E78.2.0.3", {"start": v(1009.75, 19) * mm, "mid": v(1010, 19.25) * mm, "end": v(1010.25, 19) * mm});
            skArc(sketch, "E78.2.0.4", {"start": v(1010.25, 7) * mm, "mid": v(1010, 6.75) * mm, "end": v(1009.75, 7) * mm});
            skLineSegment(sketch, "E78.3.0.0", {"start": v(1020.25, 19) * mm, "end": v(1020.25, 7) * mm});
            skLineSegment(sketch, "E78.3.0.1", {"start": v(1019.75, 19) * mm, "end": v(1019.75, 7) * mm});
            skLineSegment(sketch, "E78.3.0.2", {"start": v(1020, 19) * mm, "end": v(1020, 7) * mm});
            skArc(sketch, "E78.3.0.3", {"start": v(1019.75, 19) * mm, "mid": v(1020, 19.25) * mm, "end": v(1020.25, 19) * mm});
            skArc(sketch, "E78.3.0.4", {"start": v(1020.25, 7) * mm, "mid": v(1020, 6.75) * mm, "end": v(1019.75, 7) * mm});
            skLineSegment(sketch, "E78.4.0.0", {"start": v(1030.25, 19) * mm, "end": v(1030.25, 7) * mm});
            skLineSegment(sketch, "E78.4.0.1", {"start": v(1029.75, 19) * mm, "end": v(1029.75, 7) * mm});
            skLineSegment(sketch, "E78.4.0.2", {"start": v(1030, 19) * mm, "end": v(1030, 7) * mm});
            skArc(sketch, "E78.4.0.3", {"start": v(1029.75, 19) * mm, "mid": v(1030, 19.25) * mm, "end": v(1030.25, 19) * mm});
            skArc(sketch, "E78.4.0.4", {"start": v(1030.25, 7) * mm, "mid": v(1030, 6.75) * mm, "end": v(1029.75, 7) * mm});
            skLineSegment(sketch, "E78.5.0.0", {"start": v(1040.25, 19) * mm, "end": v(1040.25, 7) * mm});
            skLineSegment(sketch, "E78.5.0.1", {"start": v(1039.75, 19) * mm, "end": v(1039.75, 7) * mm});
            skLineSegment(sketch, "E78.5.0.2", {"start": v(1040, 19) * mm, "end": v(1040, 7) * mm});
            skArc(sketch, "E78.5.0.3", {"start": v(1039.75, 19) * mm, "mid": v(1040, 19.25) * mm, "end": v(1040.25, 19) * mm});
            skArc(sketch, "E78.5.0.4", {"start": v(1040.25, 7) * mm, "mid": v(1040, 6.75) * mm, "end": v(1039.75, 7) * mm});
            skLineSegment(sketch, "E78.6.0.0", {"start": v(1050.25, 19) * mm, "end": v(1050.25, 7) * mm});
            skLineSegment(sketch, "E78.6.0.1", {"start": v(1049.75, 19) * mm, "end": v(1049.75, 7) * mm});
            skLineSegment(sketch, "E78.6.0.2", {"start": v(1050, 19) * mm, "end": v(1050, 7) * mm});
            skArc(sketch, "E78.6.0.3", {"start": v(1049.75, 19) * mm, "mid": v(1050, 19.25) * mm, "end": v(1050.25, 19) * mm});
            skArc(sketch, "E78.6.0.4", {"start": v(1050.25, 7) * mm, "mid": v(1050, 6.75) * mm, "end": v(1049.75, 7) * mm});
            skLineSegment(sketch, "E78.7.0.0", {"start": v(1060.25, 19) * mm, "end": v(1060.25, 7) * mm});
            skLineSegment(sketch, "E78.7.0.1", {"start": v(1059.75, 19) * mm, "end": v(1059.75, 7) * mm});
            skLineSegment(sketch, "E78.7.0.2", {"start": v(1060, 19) * mm, "end": v(1060, 7) * mm});
            skArc(sketch, "E78.7.0.3", {"start": v(1059.75, 19) * mm, "mid": v(1060, 19.25) * mm, "end": v(1060.25, 19) * mm});
            skArc(sketch, "E78.7.0.4", {"start": v(1060.25, 7) * mm, "mid": v(1060, 6.75) * mm, "end": v(1059.75, 7) * mm});
            skLineSegment(sketch, "E78.8.0.0", {"start": v(1070.25, 19) * mm, "end": v(1070.25, 7) * mm});
            skLineSegment(sketch, "E78.8.0.1", {"start": v(1069.75, 19) * mm, "end": v(1069.75, 7) * mm});
            skLineSegment(sketch, "E78.8.0.2", {"start": v(1070, 19) * mm, "end": v(1070, 7) * mm});
            skArc(sketch, "E78.8.0.3", {"start": v(1069.75, 19) * mm, "mid": v(1070, 19.25) * mm, "end": v(1070.25, 19) * mm});
            skArc(sketch, "E78.8.0.4", {"start": v(1070.25, 7) * mm, "mid": v(1070, 6.75) * mm, "end": v(1069.75, 7) * mm});
            skLineSegment(sketch, "E78.9.0.0", {"start": v(1080.25, 19) * mm, "end": v(1080.25, 7) * mm});
            skLineSegment(sketch, "E78.9.0.1", {"start": v(1079.75, 19) * mm, "end": v(1079.75, 7) * mm});
            skLineSegment(sketch, "E78.9.0.2", {"start": v(1080, 19) * mm, "end": v(1080, 7) * mm});
            skArc(sketch, "E78.9.0.3", {"start": v(1079.75, 19) * mm, "mid": v(1080, 19.25) * mm, "end": v(1080.25, 19) * mm});
            skArc(sketch, "E78.9.0.4", {"start": v(1080.25, 7) * mm, "mid": v(1080, 6.75) * mm, "end": v(1079.75, 7) * mm});
            skLineSegment(sketch, "E78.10.0.0", {"start": v(1090.25, 19) * mm, "end": v(1090.25, 7) * mm});
            skLineSegment(sketch, "E78.10.0.1", {"start": v(1089.75, 19) * mm, "end": v(1089.75, 7) * mm});
            skLineSegment(sketch, "E78.10.0.2", {"start": v(1090, 19) * mm, "end": v(1090, 7) * mm});
            skArc(sketch, "E78.10.0.3", {"start": v(1089.75, 19) * mm, "mid": v(1090, 19.25) * mm, "end": v(1090.25, 19) * mm});
            skArc(sketch, "E78.10.0.4", {"start": v(1090.25, 7) * mm, "mid": v(1090, 6.75) * mm, "end": v(1089.75, 7) * mm});
            skLineSegment(sketch, "E78.11.0.0", {"start": v(1100.25, 19) * mm, "end": v(1100.25, 7) * mm});
            skLineSegment(sketch, "E78.11.0.1", {"start": v(1099.75, 19) * mm, "end": v(1099.75, 7) * mm});
            skLineSegment(sketch, "E78.11.0.2", {"start": v(1100, 19) * mm, "end": v(1100, 7) * mm});
            skArc(sketch, "E78.11.0.3", {"start": v(1099.75, 19) * mm, "mid": v(1100, 19.25) * mm, "end": v(1100.25, 19) * mm});
            skArc(sketch, "E78.11.0.4", {"start": v(1100.25, 7) * mm, "mid": v(1100, 6.75) * mm, "end": v(1099.75, 7) * mm});
            skLineSegment(sketch, "E78.12.0.0", {"start": v(1110.25, 19) * mm, "end": v(1110.25, 7) * mm});
            skLineSegment(sketch, "E78.12.0.1", {"start": v(1109.75, 19) * mm, "end": v(1109.75, 7) * mm});
            skLineSegment(sketch, "E78.12.0.2", {"start": v(1110, 19) * mm, "end": v(1110, 7) * mm});
            skArc(sketch, "E78.12.0.3", {"start": v(1109.75, 19) * mm, "mid": v(1110, 19.25) * mm, "end": v(1110.25, 19) * mm});
            skArc(sketch, "E78.12.0.4", {"start": v(1110.25, 7) * mm, "mid": v(1110, 6.75) * mm, "end": v(1109.75, 7) * mm});
            skLineSegment(sketch, "E78.13.0.0", {"start": v(1120.25, 19) * mm, "end": v(1120.25, 7) * mm});
            skLineSegment(sketch, "E78.13.0.1", {"start": v(1119.75, 19) * mm, "end": v(1119.75, 7) * mm});
            skLineSegment(sketch, "E78.13.0.2", {"start": v(1120, 19) * mm, "end": v(1120, 7) * mm});
            skArc(sketch, "E78.13.0.3", {"start": v(1119.75, 19) * mm, "mid": v(1120, 19.25) * mm, "end": v(1120.25, 19) * mm});
            skArc(sketch, "E78.13.0.4", {"start": v(1120.25, 7) * mm, "mid": v(1120, 6.75) * mm, "end": v(1119.75, 7) * mm});
            skLineSegment(sketch, "E78.14.0.0", {"start": v(1130.25, 19) * mm, "end": v(1130.25, 7) * mm});
            skLineSegment(sketch, "E78.14.0.1", {"start": v(1129.75, 19) * mm, "end": v(1129.75, 7) * mm});
            skLineSegment(sketch, "E78.14.0.2", {"start": v(1130, 19) * mm, "end": v(1130, 7) * mm});
            skArc(sketch, "E78.14.0.3", {"start": v(1129.75, 19) * mm, "mid": v(1130, 19.25) * mm, "end": v(1130.25, 19) * mm});
            skArc(sketch, "E78.14.0.4", {"start": v(1130.25, 7) * mm, "mid": v(1130, 6.75) * mm, "end": v(1129.75, 7) * mm});
            skLineSegment(sketch, "E78.15.0.0", {"start": v(1140.25, 19) * mm, "end": v(1140.25, 7) * mm});
            skLineSegment(sketch, "E78.15.0.1", {"start": v(1139.75, 19) * mm, "end": v(1139.75, 7) * mm});
            skLineSegment(sketch, "E78.15.0.2", {"start": v(1140, 19) * mm, "end": v(1140, 7) * mm});
            skArc(sketch, "E78.15.0.3", {"start": v(1139.75, 19) * mm, "mid": v(1140, 19.25) * mm, "end": v(1140.25, 19) * mm});
            skArc(sketch, "E78.15.0.4", {"start": v(1140.25, 7) * mm, "mid": v(1140, 6.75) * mm, "end": v(1139.75, 7) * mm});
            skLineSegment(sketch, "E78.16.0.0", {"start": v(1150.25, 19) * mm, "end": v(1150.25, 7) * mm});
            skLineSegment(sketch, "E78.16.0.1", {"start": v(1149.75, 19) * mm, "end": v(1149.75, 7) * mm});
            skLineSegment(sketch, "E78.16.0.2", {"start": v(1150, 19) * mm, "end": v(1150, 7) * mm});
            skArc(sketch, "E78.16.0.3", {"start": v(1149.75, 19) * mm, "mid": v(1150, 19.25) * mm, "end": v(1150.25, 19) * mm});
            skArc(sketch, "E78.16.0.4", {"start": v(1150.25, 7) * mm, "mid": v(1150, 6.75) * mm, "end": v(1149.75, 7) * mm});
            skLineSegment(sketch, "E78.17.0.0", {"start": v(1160.25, 19) * mm, "end": v(1160.25, 7) * mm});
            skLineSegment(sketch, "E78.17.0.1", {"start": v(1159.75, 19) * mm, "end": v(1159.75, 7) * mm});
            skLineSegment(sketch, "E78.17.0.2", {"start": v(1160, 19) * mm, "end": v(1160, 7) * mm});
            skArc(sketch, "E78.17.0.3", {"start": v(1159.75, 19) * mm, "mid": v(1160, 19.25) * mm, "end": v(1160.25, 19) * mm});
            skArc(sketch, "E78.17.0.4", {"start": v(1160.25, 7) * mm, "mid": v(1160, 6.75) * mm, "end": v(1159.75, 7) * mm});
            skLineSegment(sketch, "E78.18.0.0", {"start": v(1170.25, 19) * mm, "end": v(1170.25, 7) * mm});
            skLineSegment(sketch, "E78.18.0.1", {"start": v(1169.75, 19) * mm, "end": v(1169.75, 7) * mm});
            skLineSegment(sketch, "E78.18.0.2", {"start": v(1170, 19) * mm, "end": v(1170, 7) * mm});
            skArc(sketch, "E78.18.0.3", {"start": v(1169.75, 19) * mm, "mid": v(1170, 19.25) * mm, "end": v(1170.25, 19) * mm});
            skArc(sketch, "E78.18.0.4", {"start": v(1170.25, 7) * mm, "mid": v(1170, 6.75) * mm, "end": v(1169.75, 7) * mm});
            skLineSegment(sketch, "E78.19.0.0", {"start": v(1180.25, 19) * mm, "end": v(1180.25, 7) * mm});
            skLineSegment(sketch, "E78.19.0.1", {"start": v(1179.75, 19) * mm, "end": v(1179.75, 7) * mm});
            skLineSegment(sketch, "E78.19.0.2", {"start": v(1180, 19) * mm, "end": v(1180, 7) * mm});
            skArc(sketch, "E78.19.0.3", {"start": v(1179.75, 19) * mm, "mid": v(1180, 19.25) * mm, "end": v(1180.25, 19) * mm});
            skArc(sketch, "E78.19.0.4", {"start": v(1180.25, 7) * mm, "mid": v(1180, 6.75) * mm, "end": v(1179.75, 7) * mm});
            skLineSegment(sketch, "E78.direction1", {"start": v(989.75, 7) * mm, "end": v(999.75, 7) * mm, "construction": true});
            skSolve(sketch);
        }
        {
            var Q0;
            Q0 = qSketchRegion(id + "F11", true);
            extrude(context, id + "F12", {"entities" : qUnion([Q0]), "operationType" : NewBodyOperationType.REMOVE, "oppositeDirection" : true, "depth" : 0.25 * mm, "offsetDistance" : 25 * mm});
        }
        {
            var Q0;
            Q0=makeQuery(id+"F1.opExtrude","SWEPT_FACE",FACE,{"disambiguationData":[OSD([sQuery(id+"F0.wireOp",EDGE,"E1")])]});
            var sketch = newSketch(context, id + "F13", { "sketchPlane" : qUnion([Q0])});
            skCircle(sketch, "E79.0", {"center": v(-129, 0) * mm, "radius": 3 * mm});
            skSolve(sketch);
        }
        {
            var Q0;
            Q0 = qSketchRegion(id + "F13", true);
            extrude(context, id + "F14", {"entities" : qUnion([Q0]), "operationType" : NewBodyOperationType.ADD, "depth" : 3 * mm, "offsetDistance" : 25 * mm, "hasSecondDirection" : true, "secondDirectionOppositeDirection" : true, "secondDirectionDepth" : 2 * mm});
        }
        {
            var Q0;
            Q0=makeQuery(id+"F1.opExtrude","SWEPT_FACE",FACE,{"disambiguationData":[OSD([sQuery(id+"F0.wireOp",EDGE,"E3")])]});
            var sketch = newSketch(context, id + "F15", { "sketchPlane" : qUnion([Q0])});
            skLineSegment(sketch, "E80", {"start": v(0, 0) * mm, "end": v(0, 19) * mm, "construction": true});
            skLineSegment(sketch, "E81", {"start": v(0, 19) * mm, "end": v(10, 19) * mm, "construction": true});
            skLineSegment(sketch, "E82", {"start": v(5, 19) * mm, "end": v(5, 14) * mm});
            skArc(sketch, "E83.0.startCap", {"start": v(4.88, 19) * mm, "mid": v(5, 19.12) * mm, "end": v(5.13, 19) * mm});
            skArc(sketch, "E83.0.endCap", {"start": v(5.13, 14) * mm, "mid": v(5, 13.88) * mm, "end": v(4.88, 14) * mm});
            skLineSegment(sketch, "E83.0.left", {"start": v(5.12, 19) * mm, "end": v(5.12, 14) * mm});
            skLineSegment(sketch, "E83.0.right", {"start": v(4.88, 19) * mm, "end": v(4.88, 14) * mm});
            skLineSegment(sketch, "E84.1.0.0", {"start": v(14.88, 19) * mm, "end": v(14.88, 14) * mm});
            skLineSegment(sketch, "E84.1.0.1", {"start": v(15, 19) * mm, "end": v(15, 14) * mm});
            skLineSegment(sketch, "E84.1.0.2", {"start": v(15.12, 19) * mm, "end": v(15.12, 14) * mm});
            skArc(sketch, "E84.1.0.3", {"start": v(14.88, 19) * mm, "mid": v(15, 19.12) * mm, "end": v(15.13, 19) * mm});
            skArc(sketch, "E84.1.0.4", {"start": v(15.13, 14) * mm, "mid": v(15, 13.88) * mm, "end": v(14.88, 14) * mm});
            skLineSegment(sketch, "E84.2.0.0", {"start": v(24.88, 19) * mm, "end": v(24.88, 14) * mm});
            skLineSegment(sketch, "E84.2.0.1", {"start": v(25, 19) * mm, "end": v(25, 14) * mm});
            skLineSegment(sketch, "E84.2.0.2", {"start": v(25.12, 19) * mm, "end": v(25.12, 14) * mm});
            skArc(sketch, "E84.2.0.3", {"start": v(24.88, 19) * mm, "mid": v(25, 19.12) * mm, "end": v(25.13, 19) * mm});
            skArc(sketch, "E84.2.0.4", {"start": v(25.13, 14) * mm, "mid": v(25, 13.88) * mm, "end": v(24.88, 14) * mm});
            skLineSegment(sketch, "E84.3.0.0", {"start": v(34.88, 19) * mm, "end": v(34.88, 14) * mm});
            skLineSegment(sketch, "E84.3.0.1", {"start": v(35, 19) * mm, "end": v(35, 14) * mm});
            skLineSegment(sketch, "E84.3.0.2", {"start": v(35.12, 19) * mm, "end": v(35.12, 14) * mm});
            skArc(sketch, "E84.3.0.3", {"start": v(34.88, 19) * mm, "mid": v(35, 19.12) * mm, "end": v(35.13, 19) * mm});
            skArc(sketch, "E84.3.0.4", {"start": v(35.13, 14) * mm, "mid": v(35, 13.88) * mm, "end": v(34.88, 14) * mm});
            skLineSegment(sketch, "E84.4.0.0", {"start": v(44.88, 19) * mm, "end": v(44.88, 14) * mm});
            skLineSegment(sketch, "E84.4.0.1", {"start": v(45, 19) * mm, "end": v(45, 14) * mm});
            skLineSegment(sketch, "E84.4.0.2", {"start": v(45.12, 19) * mm, "end": v(45.12, 14) * mm});
            skArc(sketch, "E84.4.0.3", {"start": v(44.88, 19) * mm, "mid": v(45, 19.12) * mm, "end": v(45.13, 19) * mm});
            skArc(sketch, "E84.4.0.4", {"start": v(45.13, 14) * mm, "mid": v(45, 13.88) * mm, "end": v(44.88, 14) * mm});
            skLineSegment(sketch, "E84.5.0.0", {"start": v(54.88, 19) * mm, "end": v(54.88, 14) * mm});
            skLineSegment(sketch, "E84.5.0.1", {"start": v(55, 19) * mm, "end": v(55, 14) * mm});
            skLineSegment(sketch, "E84.5.0.2", {"start": v(55.12, 19) * mm, "end": v(55.12, 14) * mm});
            skArc(sketch, "E84.5.0.3", {"start": v(54.88, 19) * mm, "mid": v(55, 19.12) * mm, "end": v(55.13, 19) * mm});
            skArc(sketch, "E84.5.0.4", {"start": v(55.13, 14) * mm, "mid": v(55, 13.88) * mm, "end": v(54.88, 14) * mm});
            skLineSegment(sketch, "E84.6.0.0", {"start": v(64.88, 19) * mm, "end": v(64.88, 14) * mm});
            skLineSegment(sketch, "E84.6.0.1", {"start": v(65, 19) * mm, "end": v(65, 14) * mm});
            skLineSegment(sketch, "E84.6.0.2", {"start": v(65.12, 19) * mm, "end": v(65.12, 14) * mm});
            skArc(sketch, "E84.6.0.3", {"start": v(64.88, 19) * mm, "mid": v(65, 19.12) * mm, "end": v(65.13, 19) * mm});
            skArc(sketch, "E84.6.0.4", {"start": v(65.13, 14) * mm, "mid": v(65, 13.88) * mm, "end": v(64.88, 14) * mm});
            skLineSegment(sketch, "E84.7.0.0", {"start": v(74.88, 19) * mm, "end": v(74.88, 14) * mm});
            skLineSegment(sketch, "E84.7.0.1", {"start": v(75, 19) * mm, "end": v(75, 14) * mm});
            skLineSegment(sketch, "E84.7.0.2", {"start": v(75.12, 19) * mm, "end": v(75.12, 14) * mm});
            skArc(sketch, "E84.7.0.3", {"start": v(74.88, 19) * mm, "mid": v(75, 19.12) * mm, "end": v(75.13, 19) * mm});
            skArc(sketch, "E84.7.0.4", {"start": v(75.13, 14) * mm, "mid": v(75, 13.88) * mm, "end": v(74.88, 14) * mm});
            skLineSegment(sketch, "E84.8.0.0", {"start": v(84.88, 19) * mm, "end": v(84.88, 14) * mm});
            skLineSegment(sketch, "E84.8.0.1", {"start": v(85, 19) * mm, "end": v(85, 14) * mm});
            skLineSegment(sketch, "E84.8.0.2", {"start": v(85.12, 19) * mm, "end": v(85.12, 14) * mm});
            skArc(sketch, "E84.8.0.3", {"start": v(84.88, 19) * mm, "mid": v(85, 19.12) * mm, "end": v(85.13, 19) * mm});
            skArc(sketch, "E84.8.0.4", {"start": v(85.13, 14) * mm, "mid": v(85, 13.88) * mm, "end": v(84.88, 14) * mm});
            skLineSegment(sketch, "E84.9.0.0", {"start": v(94.88, 19) * mm, "end": v(94.88, 14) * mm});
            skLineSegment(sketch, "E84.9.0.1", {"start": v(95, 19) * mm, "end": v(95, 14) * mm});
            skLineSegment(sketch, "E84.9.0.2", {"start": v(95.12, 19) * mm, "end": v(95.12, 14) * mm});
            skArc(sketch, "E84.9.0.3", {"start": v(94.88, 19) * mm, "mid": v(95, 19.12) * mm, "end": v(95.13, 19) * mm});
            skArc(sketch, "E84.9.0.4", {"start": v(95.13, 14) * mm, "mid": v(95, 13.88) * mm, "end": v(94.88, 14) * mm});
            skLineSegment(sketch, "E84.10.0.0", {"start": v(104.88, 19) * mm, "end": v(104.88, 14) * mm});
            skLineSegment(sketch, "E84.10.0.1", {"start": v(105, 19) * mm, "end": v(105, 14) * mm});
            skLineSegment(sketch, "E84.10.0.2", {"start": v(105.12, 19) * mm, "end": v(105.12, 14) * mm});
            skArc(sketch, "E84.10.0.3", {"start": v(104.88, 19) * mm, "mid": v(105, 19.12) * mm, "end": v(105.13, 19) * mm});
            skArc(sketch, "E84.10.0.4", {"start": v(105.13, 14) * mm, "mid": v(105, 13.88) * mm, "end": v(104.88, 14) * mm});
            skLineSegment(sketch, "E84.11.0.0", {"start": v(114.88, 19) * mm, "end": v(114.88, 14) * mm});
            skLineSegment(sketch, "E84.11.0.1", {"start": v(115, 19) * mm, "end": v(115, 14) * mm});
            skLineSegment(sketch, "E84.11.0.2", {"start": v(115.12, 19) * mm, "end": v(115.12, 14) * mm});
            skArc(sketch, "E84.11.0.3", {"start": v(114.88, 19) * mm, "mid": v(115, 19.12) * mm, "end": v(115.13, 19) * mm});
            skArc(sketch, "E84.11.0.4", {"start": v(115.13, 14) * mm, "mid": v(115, 13.88) * mm, "end": v(114.88, 14) * mm});
            skLineSegment(sketch, "E84.12.0.0", {"start": v(124.88, 19) * mm, "end": v(124.88, 14) * mm});
            skLineSegment(sketch, "E84.12.0.1", {"start": v(125, 19) * mm, "end": v(125, 14) * mm});
            skLineSegment(sketch, "E84.12.0.2", {"start": v(125.12, 19) * mm, "end": v(125.12, 14) * mm});
            skArc(sketch, "E84.12.0.3", {"start": v(124.88, 19) * mm, "mid": v(125, 19.12) * mm, "end": v(125.13, 19) * mm});
            skArc(sketch, "E84.12.0.4", {"start": v(125.13, 14) * mm, "mid": v(125, 13.88) * mm, "end": v(124.88, 14) * mm});
            skLineSegment(sketch, "E84.13.0.0", {"start": v(134.88, 19) * mm, "end": v(134.88, 14) * mm});
            skLineSegment(sketch, "E84.13.0.1", {"start": v(135, 19) * mm, "end": v(135, 14) * mm});
            skLineSegment(sketch, "E84.13.0.2", {"start": v(135.12, 19) * mm, "end": v(135.12, 14) * mm});
            skArc(sketch, "E84.13.0.3", {"start": v(134.88, 19) * mm, "mid": v(135, 19.12) * mm, "end": v(135.13, 19) * mm});
            skArc(sketch, "E84.13.0.4", {"start": v(135.13, 14) * mm, "mid": v(135, 13.88) * mm, "end": v(134.88, 14) * mm});
            skLineSegment(sketch, "E84.14.0.0", {"start": v(144.88, 19) * mm, "end": v(144.88, 14) * mm});
            skLineSegment(sketch, "E84.14.0.1", {"start": v(145, 19) * mm, "end": v(145, 14) * mm});
            skLineSegment(sketch, "E84.14.0.2", {"start": v(145.12, 19) * mm, "end": v(145.12, 14) * mm});
            skArc(sketch, "E84.14.0.3", {"start": v(144.88, 19) * mm, "mid": v(145, 19.12) * mm, "end": v(145.13, 19) * mm});
            skArc(sketch, "E84.14.0.4", {"start": v(145.12, 14) * mm, "mid": v(145, 13.88) * mm, "end": v(144.88, 14) * mm});
            skLineSegment(sketch, "E84.15.0.0", {"start": v(154.88, 19) * mm, "end": v(154.88, 14) * mm});
            skLineSegment(sketch, "E84.15.0.1", {"start": v(155, 19) * mm, "end": v(155, 14) * mm});
            skLineSegment(sketch, "E84.15.0.2", {"start": v(155.12, 19) * mm, "end": v(155.12, 14) * mm});
            skArc(sketch, "E84.15.0.3", {"start": v(154.88, 19) * mm, "mid": v(155, 19.12) * mm, "end": v(155.13, 19) * mm});
            skArc(sketch, "E84.15.0.4", {"start": v(155.12, 14) * mm, "mid": v(155, 13.88) * mm, "end": v(154.88, 14) * mm});
            skLineSegment(sketch, "E84.16.0.0", {"start": v(164.88, 19) * mm, "end": v(164.88, 14) * mm});
            skLineSegment(sketch, "E84.16.0.1", {"start": v(165, 19) * mm, "end": v(165, 14) * mm});
            skLineSegment(sketch, "E84.16.0.2", {"start": v(165.12, 19) * mm, "end": v(165.12, 14) * mm});
            skArc(sketch, "E84.16.0.3", {"start": v(164.88, 19) * mm, "mid": v(165, 19.12) * mm, "end": v(165.13, 19) * mm});
            skArc(sketch, "E84.16.0.4", {"start": v(165.13, 14) * mm, "mid": v(165, 13.88) * mm, "end": v(164.88, 14) * mm});
            skLineSegment(sketch, "E84.17.0.0", {"start": v(174.88, 19) * mm, "end": v(174.88, 14) * mm});
            skLineSegment(sketch, "E84.17.0.1", {"start": v(175, 19) * mm, "end": v(175, 14) * mm});
            skLineSegment(sketch, "E84.17.0.2", {"start": v(175.12, 19) * mm, "end": v(175.12, 14) * mm});
            skArc(sketch, "E84.17.0.3", {"start": v(174.88, 19) * mm, "mid": v(175, 19.12) * mm, "end": v(175.13, 19) * mm});
            skArc(sketch, "E84.17.0.4", {"start": v(175.13, 14) * mm, "mid": v(175, 13.88) * mm, "end": v(174.88, 14) * mm});
            skLineSegment(sketch, "E84.18.0.0", {"start": v(184.88, 19) * mm, "end": v(184.88, 14) * mm});
            skLineSegment(sketch, "E84.18.0.1", {"start": v(185, 19) * mm, "end": v(185, 14) * mm});
            skLineSegment(sketch, "E84.18.0.2", {"start": v(185.12, 19) * mm, "end": v(185.12, 14) * mm});
            skArc(sketch, "E84.18.0.3", {"start": v(184.88, 19) * mm, "mid": v(185, 19.12) * mm, "end": v(185.13, 19) * mm});
            skArc(sketch, "E84.18.0.4", {"start": v(185.13, 14) * mm, "mid": v(185, 13.88) * mm, "end": v(184.88, 14) * mm});
            skLineSegment(sketch, "E84.19.0.0", {"start": v(194.88, 19) * mm, "end": v(194.88, 14) * mm});
            skLineSegment(sketch, "E84.19.0.1", {"start": v(195, 19) * mm, "end": v(195, 14) * mm});
            skLineSegment(sketch, "E84.19.0.2", {"start": v(195.12, 19) * mm, "end": v(195.12, 14) * mm});
            skArc(sketch, "E84.19.0.3", {"start": v(194.88, 19) * mm, "mid": v(195, 19.12) * mm, "end": v(195.13, 19) * mm});
            skArc(sketch, "E84.19.0.4", {"start": v(195.13, 14) * mm, "mid": v(195, 13.88) * mm, "end": v(194.88, 14) * mm});
            skLineSegment(sketch, "E84.20.0.0", {"start": v(204.88, 19) * mm, "end": v(204.88, 14) * mm});
            skLineSegment(sketch, "E84.20.0.1", {"start": v(205, 19) * mm, "end": v(205, 14) * mm});
            skLineSegment(sketch, "E84.20.0.2", {"start": v(205.12, 19) * mm, "end": v(205.12, 14) * mm});
            skArc(sketch, "E84.20.0.3", {"start": v(204.88, 19) * mm, "mid": v(205, 19.12) * mm, "end": v(205.13, 19) * mm});
            skArc(sketch, "E84.20.0.4", {"start": v(205.13, 14) * mm, "mid": v(205, 13.88) * mm, "end": v(204.88, 14) * mm});
            skLineSegment(sketch, "E84.21.0.0", {"start": v(214.88, 19) * mm, "end": v(214.88, 14) * mm});
            skLineSegment(sketch, "E84.21.0.1", {"start": v(215, 19) * mm, "end": v(215, 14) * mm});
            skLineSegment(sketch, "E84.21.0.2", {"start": v(215.12, 19) * mm, "end": v(215.12, 14) * mm});
            skArc(sketch, "E84.21.0.3", {"start": v(214.88, 19) * mm, "mid": v(215, 19.12) * mm, "end": v(215.13, 19) * mm});
            skArc(sketch, "E84.21.0.4", {"start": v(215.13, 14) * mm, "mid": v(215, 13.88) * mm, "end": v(214.88, 14) * mm});
            skLineSegment(sketch, "E84.22.0.0", {"start": v(224.88, 19) * mm, "end": v(224.88, 14) * mm});
            skLineSegment(sketch, "E84.22.0.1", {"start": v(225, 19) * mm, "end": v(225, 14) * mm});
            skLineSegment(sketch, "E84.22.0.2", {"start": v(225.12, 19) * mm, "end": v(225.12, 14) * mm});
            skArc(sketch, "E84.22.0.3", {"start": v(224.88, 19) * mm, "mid": v(225, 19.12) * mm, "end": v(225.13, 19) * mm});
            skArc(sketch, "E84.22.0.4", {"start": v(225.13, 14) * mm, "mid": v(225, 13.88) * mm, "end": v(224.88, 14) * mm});
            skLineSegment(sketch, "E84.23.0.0", {"start": v(234.88, 19) * mm, "end": v(234.88, 14) * mm});
            skLineSegment(sketch, "E84.23.0.1", {"start": v(235, 19) * mm, "end": v(235, 14) * mm});
            skLineSegment(sketch, "E84.23.0.2", {"start": v(235.12, 19) * mm, "end": v(235.12, 14) * mm});
            skArc(sketch, "E84.23.0.3", {"start": v(234.88, 19) * mm, "mid": v(235, 19.12) * mm, "end": v(235.13, 19) * mm});
            skArc(sketch, "E84.23.0.4", {"start": v(235.13, 14) * mm, "mid": v(235, 13.88) * mm, "end": v(234.88, 14) * mm});
            skLineSegment(sketch, "E84.24.0.0", {"start": v(244.88, 19) * mm, "end": v(244.88, 14) * mm});
            skLineSegment(sketch, "E84.24.0.1", {"start": v(245, 19) * mm, "end": v(245, 14) * mm});
            skLineSegment(sketch, "E84.24.0.2", {"start": v(245.12, 19) * mm, "end": v(245.12, 14) * mm});
            skArc(sketch, "E84.24.0.3", {"start": v(244.88, 19) * mm, "mid": v(245, 19.12) * mm, "end": v(245.13, 19) * mm});
            skArc(sketch, "E84.24.0.4", {"start": v(245.13, 14) * mm, "mid": v(245, 13.88) * mm, "end": v(244.88, 14) * mm});
            skLineSegment(sketch, "E84.25.0.0", {"start": v(254.88, 19) * mm, "end": v(254.88, 14) * mm});
            skLineSegment(sketch, "E84.25.0.1", {"start": v(255, 19) * mm, "end": v(255, 14) * mm});
            skLineSegment(sketch, "E84.25.0.2", {"start": v(255.12, 19) * mm, "end": v(255.12, 14) * mm});
            skArc(sketch, "E84.25.0.3", {"start": v(254.88, 19) * mm, "mid": v(255, 19.12) * mm, "end": v(255.13, 19) * mm});
            skArc(sketch, "E84.25.0.4", {"start": v(255.13, 14) * mm, "mid": v(255, 13.88) * mm, "end": v(254.88, 14) * mm});
            skLineSegment(sketch, "E84.26.0.0", {"start": v(264.88, 19) * mm, "end": v(264.88, 14) * mm});
            skLineSegment(sketch, "E84.26.0.1", {"start": v(265, 19) * mm, "end": v(265, 14) * mm});
            skLineSegment(sketch, "E84.26.0.2", {"start": v(265.12, 19) * mm, "end": v(265.12, 14) * mm});
            skArc(sketch, "E84.26.0.3", {"start": v(264.88, 19) * mm, "mid": v(265, 19.12) * mm, "end": v(265.13, 19) * mm});
            skArc(sketch, "E84.26.0.4", {"start": v(265.13, 14) * mm, "mid": v(265, 13.88) * mm, "end": v(264.88, 14) * mm});
            skLineSegment(sketch, "E84.27.0.0", {"start": v(274.88, 19) * mm, "end": v(274.88, 14) * mm});
            skLineSegment(sketch, "E84.27.0.1", {"start": v(275, 19) * mm, "end": v(275, 14) * mm});
            skLineSegment(sketch, "E84.27.0.2", {"start": v(275.12, 19) * mm, "end": v(275.12, 14) * mm});
            skArc(sketch, "E84.27.0.3", {"start": v(274.88, 19) * mm, "mid": v(275, 19.12) * mm, "end": v(275.13, 19) * mm});
            skArc(sketch, "E84.27.0.4", {"start": v(275.13, 14) * mm, "mid": v(275, 13.88) * mm, "end": v(274.88, 14) * mm});
            skLineSegment(sketch, "E84.28.0.0", {"start": v(284.88, 19) * mm, "end": v(284.88, 14) * mm});
            skLineSegment(sketch, "E84.28.0.1", {"start": v(285, 19) * mm, "end": v(285, 14) * mm});
            skLineSegment(sketch, "E84.28.0.2", {"start": v(285.12, 19) * mm, "end": v(285.12, 14) * mm});
            skArc(sketch, "E84.28.0.3", {"start": v(284.88, 19) * mm, "mid": v(285, 19.12) * mm, "end": v(285.13, 19) * mm});
            skArc(sketch, "E84.28.0.4", {"start": v(285.12, 14) * mm, "mid": v(285, 13.88) * mm, "end": v(284.88, 14) * mm});
            skLineSegment(sketch, "E84.29.0.0", {"start": v(294.88, 19) * mm, "end": v(294.88, 14) * mm});
            skLineSegment(sketch, "E84.29.0.1", {"start": v(295, 19) * mm, "end": v(295, 14) * mm});
            skLineSegment(sketch, "E84.29.0.2", {"start": v(295.12, 19) * mm, "end": v(295.12, 14) * mm});
            skArc(sketch, "E84.29.0.3", {"start": v(294.88, 19) * mm, "mid": v(295, 19.12) * mm, "end": v(295.13, 19) * mm});
            skArc(sketch, "E84.29.0.4", {"start": v(295.12, 14) * mm, "mid": v(295, 13.88) * mm, "end": v(294.88, 14) * mm});
            skLineSegment(sketch, "E84.30.0.0", {"start": v(304.88, 19) * mm, "end": v(304.88, 14) * mm});
            skLineSegment(sketch, "E84.30.0.1", {"start": v(305, 19) * mm, "end": v(305, 14) * mm});
            skLineSegment(sketch, "E84.30.0.2", {"start": v(305.12, 19) * mm, "end": v(305.12, 14) * mm});
            skArc(sketch, "E84.30.0.3", {"start": v(304.88, 19) * mm, "mid": v(305, 19.12) * mm, "end": v(305.13, 19) * mm});
            skArc(sketch, "E84.30.0.4", {"start": v(305.13, 14) * mm, "mid": v(305, 13.88) * mm, "end": v(304.88, 14) * mm});
            skLineSegment(sketch, "E84.31.0.0", {"start": v(314.88, 19) * mm, "end": v(314.88, 14) * mm});
            skLineSegment(sketch, "E84.31.0.1", {"start": v(315, 19) * mm, "end": v(315, 14) * mm});
            skLineSegment(sketch, "E84.31.0.2", {"start": v(315.12, 19) * mm, "end": v(315.12, 14) * mm});
            skArc(sketch, "E84.31.0.3", {"start": v(314.88, 19) * mm, "mid": v(315, 19.12) * mm, "end": v(315.13, 19) * mm});
            skArc(sketch, "E84.31.0.4", {"start": v(315.13, 14) * mm, "mid": v(315, 13.88) * mm, "end": v(314.88, 14) * mm});
            skLineSegment(sketch, "E84.32.0.0", {"start": v(324.88, 19) * mm, "end": v(324.88, 14) * mm});
            skLineSegment(sketch, "E84.32.0.1", {"start": v(325, 19) * mm, "end": v(325, 14) * mm});
            skLineSegment(sketch, "E84.32.0.2", {"start": v(325.12, 19) * mm, "end": v(325.12, 14) * mm});
            skArc(sketch, "E84.32.0.3", {"start": v(324.88, 19) * mm, "mid": v(325, 19.12) * mm, "end": v(325.13, 19) * mm});
            skArc(sketch, "E84.32.0.4", {"start": v(325.13, 14) * mm, "mid": v(325, 13.88) * mm, "end": v(324.88, 14) * mm});
            skLineSegment(sketch, "E84.33.0.0", {"start": v(334.88, 19) * mm, "end": v(334.88, 14) * mm});
            skLineSegment(sketch, "E84.33.0.1", {"start": v(335, 19) * mm, "end": v(335, 14) * mm});
            skLineSegment(sketch, "E84.33.0.2", {"start": v(335.12, 19) * mm, "end": v(335.12, 14) * mm});
            skArc(sketch, "E84.33.0.3", {"start": v(334.88, 19) * mm, "mid": v(335, 19.12) * mm, "end": v(335.13, 19) * mm});
            skArc(sketch, "E84.33.0.4", {"start": v(335.13, 14) * mm, "mid": v(335, 13.88) * mm, "end": v(334.88, 14) * mm});
            skLineSegment(sketch, "E84.34.0.0", {"start": v(344.88, 19) * mm, "end": v(344.88, 14) * mm});
            skLineSegment(sketch, "E84.34.0.1", {"start": v(345, 19) * mm, "end": v(345, 14) * mm});
            skLineSegment(sketch, "E84.34.0.2", {"start": v(345.12, 19) * mm, "end": v(345.12, 14) * mm});
            skArc(sketch, "E84.34.0.3", {"start": v(344.88, 19) * mm, "mid": v(345, 19.12) * mm, "end": v(345.13, 19) * mm});
            skArc(sketch, "E84.34.0.4", {"start": v(345.13, 14) * mm, "mid": v(345, 13.88) * mm, "end": v(344.88, 14) * mm});
            skLineSegment(sketch, "E84.35.0.0", {"start": v(354.88, 19) * mm, "end": v(354.88, 14) * mm});
            skLineSegment(sketch, "E84.35.0.1", {"start": v(355, 19) * mm, "end": v(355, 14) * mm});
            skLineSegment(sketch, "E84.35.0.2", {"start": v(355.12, 19) * mm, "end": v(355.12, 14) * mm});
            skArc(sketch, "E84.35.0.3", {"start": v(354.88, 19) * mm, "mid": v(355, 19.12) * mm, "end": v(355.13, 19) * mm});
            skArc(sketch, "E84.35.0.4", {"start": v(355.13, 14) * mm, "mid": v(355, 13.88) * mm, "end": v(354.88, 14) * mm});
            skLineSegment(sketch, "E84.36.0.0", {"start": v(364.88, 19) * mm, "end": v(364.88, 14) * mm});
            skLineSegment(sketch, "E84.36.0.1", {"start": v(365, 19) * mm, "end": v(365, 14) * mm});
            skLineSegment(sketch, "E84.36.0.2", {"start": v(365.12, 19) * mm, "end": v(365.12, 14) * mm});
            skArc(sketch, "E84.36.0.3", {"start": v(364.88, 19) * mm, "mid": v(365, 19.12) * mm, "end": v(365.13, 19) * mm});
            skArc(sketch, "E84.36.0.4", {"start": v(365.13, 14) * mm, "mid": v(365, 13.88) * mm, "end": v(364.88, 14) * mm});
            skLineSegment(sketch, "E84.37.0.0", {"start": v(374.88, 19) * mm, "end": v(374.88, 14) * mm});
            skLineSegment(sketch, "E84.37.0.1", {"start": v(375, 19) * mm, "end": v(375, 14) * mm});
            skLineSegment(sketch, "E84.37.0.2", {"start": v(375.12, 19) * mm, "end": v(375.12, 14) * mm});
            skArc(sketch, "E84.37.0.3", {"start": v(374.88, 19) * mm, "mid": v(375, 19.12) * mm, "end": v(375.13, 19) * mm});
            skArc(sketch, "E84.37.0.4", {"start": v(375.13, 14) * mm, "mid": v(375, 13.88) * mm, "end": v(374.88, 14) * mm});
            skLineSegment(sketch, "E84.38.0.0", {"start": v(384.88, 19) * mm, "end": v(384.88, 14) * mm});
            skLineSegment(sketch, "E84.38.0.1", {"start": v(385, 19) * mm, "end": v(385, 14) * mm});
            skLineSegment(sketch, "E84.38.0.2", {"start": v(385.12, 19) * mm, "end": v(385.12, 14) * mm});
            skArc(sketch, "E84.38.0.3", {"start": v(384.88, 19) * mm, "mid": v(385, 19.12) * mm, "end": v(385.13, 19) * mm});
            skArc(sketch, "E84.38.0.4", {"start": v(385.13, 14) * mm, "mid": v(385, 13.88) * mm, "end": v(384.88, 14) * mm});
            skLineSegment(sketch, "E84.39.0.0", {"start": v(394.88, 19) * mm, "end": v(394.88, 14) * mm});
            skLineSegment(sketch, "E84.39.0.1", {"start": v(395, 19) * mm, "end": v(395, 14) * mm});
            skLineSegment(sketch, "E84.39.0.2", {"start": v(395.12, 19) * mm, "end": v(395.12, 14) * mm});
            skArc(sketch, "E84.39.0.3", {"start": v(394.88, 19) * mm, "mid": v(395, 19.12) * mm, "end": v(395.13, 19) * mm});
            skArc(sketch, "E84.39.0.4", {"start": v(395.13, 14) * mm, "mid": v(395, 13.88) * mm, "end": v(394.88, 14) * mm});
            skLineSegment(sketch, "E84.40.0.0", {"start": v(404.88, 19) * mm, "end": v(404.88, 14) * mm});
            skLineSegment(sketch, "E84.40.0.1", {"start": v(405, 19) * mm, "end": v(405, 14) * mm});
            skLineSegment(sketch, "E84.40.0.2", {"start": v(405.12, 19) * mm, "end": v(405.12, 14) * mm});
            skArc(sketch, "E84.40.0.3", {"start": v(404.88, 19) * mm, "mid": v(405, 19.12) * mm, "end": v(405.13, 19) * mm});
            skArc(sketch, "E84.40.0.4", {"start": v(405.13, 14) * mm, "mid": v(405, 13.88) * mm, "end": v(404.88, 14) * mm});
            skLineSegment(sketch, "E84.41.0.0", {"start": v(414.88, 19) * mm, "end": v(414.88, 14) * mm});
            skLineSegment(sketch, "E84.41.0.1", {"start": v(415, 19) * mm, "end": v(415, 14) * mm});
            skLineSegment(sketch, "E84.41.0.2", {"start": v(415.12, 19) * mm, "end": v(415.12, 14) * mm});
            skArc(sketch, "E84.41.0.3", {"start": v(414.88, 19) * mm, "mid": v(415, 19.12) * mm, "end": v(415.13, 19) * mm});
            skArc(sketch, "E84.41.0.4", {"start": v(415.13, 14) * mm, "mid": v(415, 13.88) * mm, "end": v(414.88, 14) * mm});
            skLineSegment(sketch, "E84.42.0.0", {"start": v(424.88, 19) * mm, "end": v(424.88, 14) * mm});
            skLineSegment(sketch, "E84.42.0.1", {"start": v(425, 19) * mm, "end": v(425, 14) * mm});
            skLineSegment(sketch, "E84.42.0.2", {"start": v(425.12, 19) * mm, "end": v(425.12, 14) * mm});
            skArc(sketch, "E84.42.0.3", {"start": v(424.88, 19) * mm, "mid": v(425, 19.12) * mm, "end": v(425.13, 19) * mm});
            skArc(sketch, "E84.42.0.4", {"start": v(425.13, 14) * mm, "mid": v(425, 13.88) * mm, "end": v(424.88, 14) * mm});
            skLineSegment(sketch, "E84.43.0.0", {"start": v(434.88, 19) * mm, "end": v(434.88, 14) * mm});
            skLineSegment(sketch, "E84.43.0.1", {"start": v(435, 19) * mm, "end": v(435, 14) * mm});
            skLineSegment(sketch, "E84.43.0.2", {"start": v(435.12, 19) * mm, "end": v(435.12, 14) * mm});
            skArc(sketch, "E84.43.0.3", {"start": v(434.88, 19) * mm, "mid": v(435, 19.12) * mm, "end": v(435.13, 19) * mm});
            skArc(sketch, "E84.43.0.4", {"start": v(435.13, 14) * mm, "mid": v(435, 13.88) * mm, "end": v(434.88, 14) * mm});
            skLineSegment(sketch, "E84.44.0.0", {"start": v(444.88, 19) * mm, "end": v(444.88, 14) * mm});
            skLineSegment(sketch, "E84.44.0.1", {"start": v(445, 19) * mm, "end": v(445, 14) * mm});
            skLineSegment(sketch, "E84.44.0.2", {"start": v(445.12, 19) * mm, "end": v(445.12, 14) * mm});
            skArc(sketch, "E84.44.0.3", {"start": v(444.88, 19) * mm, "mid": v(445, 19.12) * mm, "end": v(445.13, 19) * mm});
            skArc(sketch, "E84.44.0.4", {"start": v(445.13, 14) * mm, "mid": v(445, 13.88) * mm, "end": v(444.88, 14) * mm});
            skLineSegment(sketch, "E84.45.0.0", {"start": v(454.88, 19) * mm, "end": v(454.88, 14) * mm});
            skLineSegment(sketch, "E84.45.0.1", {"start": v(455, 19) * mm, "end": v(455, 14) * mm});
            skLineSegment(sketch, "E84.45.0.2", {"start": v(455.12, 19) * mm, "end": v(455.12, 14) * mm});
            skArc(sketch, "E84.45.0.3", {"start": v(454.88, 19) * mm, "mid": v(455, 19.12) * mm, "end": v(455.13, 19) * mm});
            skArc(sketch, "E84.45.0.4", {"start": v(455.13, 14) * mm, "mid": v(455, 13.88) * mm, "end": v(454.88, 14) * mm});
            skLineSegment(sketch, "E84.46.0.0", {"start": v(464.88, 19) * mm, "end": v(464.88, 14) * mm});
            skLineSegment(sketch, "E84.46.0.1", {"start": v(465, 19) * mm, "end": v(465, 14) * mm});
            skLineSegment(sketch, "E84.46.0.2", {"start": v(465.12, 19) * mm, "end": v(465.12, 14) * mm});
            skArc(sketch, "E84.46.0.3", {"start": v(464.88, 19) * mm, "mid": v(465, 19.12) * mm, "end": v(465.13, 19) * mm});
            skArc(sketch, "E84.46.0.4", {"start": v(465.13, 14) * mm, "mid": v(465, 13.88) * mm, "end": v(464.88, 14) * mm});
            skLineSegment(sketch, "E84.47.0.0", {"start": v(474.88, 19) * mm, "end": v(474.88, 14) * mm});
            skLineSegment(sketch, "E84.47.0.1", {"start": v(475, 19) * mm, "end": v(475, 14) * mm});
            skLineSegment(sketch, "E84.47.0.2", {"start": v(475.12, 19) * mm, "end": v(475.12, 14) * mm});
            skArc(sketch, "E84.47.0.3", {"start": v(474.88, 19) * mm, "mid": v(475, 19.12) * mm, "end": v(475.13, 19) * mm});
            skArc(sketch, "E84.47.0.4", {"start": v(475.13, 14) * mm, "mid": v(475, 13.88) * mm, "end": v(474.88, 14) * mm});
            skLineSegment(sketch, "E84.48.0.0", {"start": v(484.88, 19) * mm, "end": v(484.88, 14) * mm});
            skLineSegment(sketch, "E84.48.0.1", {"start": v(485, 19) * mm, "end": v(485, 14) * mm});
            skLineSegment(sketch, "E84.48.0.2", {"start": v(485.12, 19) * mm, "end": v(485.12, 14) * mm});
            skArc(sketch, "E84.48.0.3", {"start": v(484.88, 19) * mm, "mid": v(485, 19.12) * mm, "end": v(485.13, 19) * mm});
            skArc(sketch, "E84.48.0.4", {"start": v(485.13, 14) * mm, "mid": v(485, 13.88) * mm, "end": v(484.88, 14) * mm});
            skLineSegment(sketch, "E84.49.0.0", {"start": v(494.88, 19) * mm, "end": v(494.88, 14) * mm});
            skLineSegment(sketch, "E84.49.0.1", {"start": v(495, 19) * mm, "end": v(495, 14) * mm});
            skLineSegment(sketch, "E84.49.0.2", {"start": v(495.12, 19) * mm, "end": v(495.12, 14) * mm});
            skArc(sketch, "E84.49.0.3", {"start": v(494.88, 19) * mm, "mid": v(495, 19.12) * mm, "end": v(495.13, 19) * mm});
            skArc(sketch, "E84.49.0.4", {"start": v(495.13, 14) * mm, "mid": v(495, 13.88) * mm, "end": v(494.88, 14) * mm});
            skLineSegment(sketch, "E84.50.0.0", {"start": v(504.88, 19) * mm, "end": v(504.88, 14) * mm});
            skLineSegment(sketch, "E84.50.0.1", {"start": v(505, 19) * mm, "end": v(505, 14) * mm});
            skLineSegment(sketch, "E84.50.0.2", {"start": v(505.13, 19) * mm, "end": v(505.13, 14) * mm});
            skArc(sketch, "E84.50.0.3", {"start": v(504.88, 19) * mm, "mid": v(505, 19.12) * mm, "end": v(505.13, 19) * mm});
            skArc(sketch, "E84.50.0.4", {"start": v(505.13, 14) * mm, "mid": v(505, 13.88) * mm, "end": v(504.88, 14) * mm});
            skLineSegment(sketch, "E84.51.0.0", {"start": v(514.88, 19) * mm, "end": v(514.88, 14) * mm});
            skLineSegment(sketch, "E84.51.0.1", {"start": v(515, 19) * mm, "end": v(515, 14) * mm});
            skLineSegment(sketch, "E84.51.0.2", {"start": v(515.12, 19) * mm, "end": v(515.12, 14) * mm});
            skArc(sketch, "E84.51.0.3", {"start": v(514.88, 19) * mm, "mid": v(515, 19.12) * mm, "end": v(515.13, 19) * mm});
            skArc(sketch, "E84.51.0.4", {"start": v(515.13, 14) * mm, "mid": v(515, 13.88) * mm, "end": v(514.88, 14) * mm});
            skLineSegment(sketch, "E84.52.0.0", {"start": v(524.88, 19) * mm, "end": v(524.88, 14) * mm});
            skLineSegment(sketch, "E84.52.0.1", {"start": v(525, 19) * mm, "end": v(525, 14) * mm});
            skLineSegment(sketch, "E84.52.0.2", {"start": v(525.13, 19) * mm, "end": v(525.13, 14) * mm});
            skArc(sketch, "E84.52.0.3", {"start": v(524.88, 19) * mm, "mid": v(525, 19.12) * mm, "end": v(525.13, 19) * mm});
            skArc(sketch, "E84.52.0.4", {"start": v(525.13, 14) * mm, "mid": v(525, 13.88) * mm, "end": v(524.88, 14) * mm});
            skLineSegment(sketch, "E84.53.0.0", {"start": v(534.88, 19) * mm, "end": v(534.88, 14) * mm});
            skLineSegment(sketch, "E84.53.0.1", {"start": v(535, 19) * mm, "end": v(535, 14) * mm});
            skLineSegment(sketch, "E84.53.0.2", {"start": v(535.13, 19) * mm, "end": v(535.13, 14) * mm});
            skArc(sketch, "E84.53.0.3", {"start": v(534.88, 19) * mm, "mid": v(535, 19.12) * mm, "end": v(535.13, 19) * mm});
            skArc(sketch, "E84.53.0.4", {"start": v(535.13, 14) * mm, "mid": v(535, 13.88) * mm, "end": v(534.88, 14) * mm});
            skLineSegment(sketch, "E84.54.0.0", {"start": v(544.88, 19) * mm, "end": v(544.88, 14) * mm});
            skLineSegment(sketch, "E84.54.0.1", {"start": v(545, 19) * mm, "end": v(545, 14) * mm});
            skLineSegment(sketch, "E84.54.0.2", {"start": v(545.13, 19) * mm, "end": v(545.13, 14) * mm});
            skArc(sketch, "E84.54.0.3", {"start": v(544.88, 19) * mm, "mid": v(545, 19.12) * mm, "end": v(545.13, 19) * mm});
            skArc(sketch, "E84.54.0.4", {"start": v(545.13, 14) * mm, "mid": v(545, 13.88) * mm, "end": v(544.88, 14) * mm});
            skLineSegment(sketch, "E84.55.0.0", {"start": v(554.88, 19) * mm, "end": v(554.88, 14) * mm});
            skLineSegment(sketch, "E84.55.0.1", {"start": v(555, 19) * mm, "end": v(555, 14) * mm});
            skLineSegment(sketch, "E84.55.0.2", {"start": v(555.13, 19) * mm, "end": v(555.13, 14) * mm});
            skArc(sketch, "E84.55.0.3", {"start": v(554.88, 19) * mm, "mid": v(555, 19.12) * mm, "end": v(555.13, 19) * mm});
            skArc(sketch, "E84.55.0.4", {"start": v(555.13, 14) * mm, "mid": v(555, 13.88) * mm, "end": v(554.88, 14) * mm});
            skLineSegment(sketch, "E84.56.0.0", {"start": v(564.88, 19) * mm, "end": v(564.88, 14) * mm});
            skLineSegment(sketch, "E84.56.0.1", {"start": v(565, 19) * mm, "end": v(565, 14) * mm});
            skLineSegment(sketch, "E84.56.0.2", {"start": v(565.12, 19) * mm, "end": v(565.12, 14) * mm});
            skArc(sketch, "E84.56.0.3", {"start": v(564.88, 19) * mm, "mid": v(565, 19.12) * mm, "end": v(565.13, 19) * mm});
            skArc(sketch, "E84.56.0.4", {"start": v(565.13, 14) * mm, "mid": v(565, 13.88) * mm, "end": v(564.88, 14) * mm});
            skLineSegment(sketch, "E84.57.0.0", {"start": v(574.88, 19) * mm, "end": v(574.88, 14) * mm});
            skLineSegment(sketch, "E84.57.0.1", {"start": v(575, 19) * mm, "end": v(575, 14) * mm});
            skLineSegment(sketch, "E84.57.0.2", {"start": v(575.12, 19) * mm, "end": v(575.12, 14) * mm});
            skArc(sketch, "E84.57.0.3", {"start": v(574.88, 19) * mm, "mid": v(575, 19.12) * mm, "end": v(575.13, 19) * mm});
            skArc(sketch, "E84.57.0.4", {"start": v(575.13, 14) * mm, "mid": v(575, 13.88) * mm, "end": v(574.88, 14) * mm});
            skLineSegment(sketch, "E84.58.0.0", {"start": v(584.88, 19) * mm, "end": v(584.88, 14) * mm});
            skLineSegment(sketch, "E84.58.0.1", {"start": v(585, 19) * mm, "end": v(585, 14) * mm});
            skLineSegment(sketch, "E84.58.0.2", {"start": v(585.12, 19) * mm, "end": v(585.12, 14) * mm});
            skArc(sketch, "E84.58.0.3", {"start": v(584.88, 19) * mm, "mid": v(585, 19.12) * mm, "end": v(585.13, 19) * mm});
            skArc(sketch, "E84.58.0.4", {"start": v(585.13, 14) * mm, "mid": v(585, 13.88) * mm, "end": v(584.88, 14) * mm});
            skLineSegment(sketch, "E84.59.0.0", {"start": v(594.88, 19) * mm, "end": v(594.88, 14) * mm});
            skLineSegment(sketch, "E84.59.0.1", {"start": v(595, 19) * mm, "end": v(595, 14) * mm});
            skLineSegment(sketch, "E84.59.0.2", {"start": v(595.12, 19) * mm, "end": v(595.12, 14) * mm});
            skArc(sketch, "E84.59.0.3", {"start": v(594.88, 19) * mm, "mid": v(595, 19.12) * mm, "end": v(595.13, 19) * mm});
            skArc(sketch, "E84.59.0.4", {"start": v(595.13, 14) * mm, "mid": v(595, 13.88) * mm, "end": v(594.88, 14) * mm});
            skLineSegment(sketch, "E84.60.0.0", {"start": v(604.88, 19) * mm, "end": v(604.88, 14) * mm});
            skLineSegment(sketch, "E84.60.0.1", {"start": v(605, 19) * mm, "end": v(605, 14) * mm});
            skLineSegment(sketch, "E84.60.0.2", {"start": v(605.12, 19) * mm, "end": v(605.12, 14) * mm});
            skArc(sketch, "E84.60.0.3", {"start": v(604.88, 19) * mm, "mid": v(605, 19.12) * mm, "end": v(605.13, 19) * mm});
            skArc(sketch, "E84.60.0.4", {"start": v(605.13, 14) * mm, "mid": v(605, 13.88) * mm, "end": v(604.88, 14) * mm});
            skLineSegment(sketch, "E84.61.0.0", {"start": v(614.88, 19) * mm, "end": v(614.88, 14) * mm});
            skLineSegment(sketch, "E84.61.0.1", {"start": v(615, 19) * mm, "end": v(615, 14) * mm});
            skLineSegment(sketch, "E84.61.0.2", {"start": v(615.12, 19) * mm, "end": v(615.12, 14) * mm});
            skArc(sketch, "E84.61.0.3", {"start": v(614.88, 19) * mm, "mid": v(615, 19.12) * mm, "end": v(615.13, 19) * mm});
            skArc(sketch, "E84.61.0.4", {"start": v(615.13, 14) * mm, "mid": v(615, 13.88) * mm, "end": v(614.88, 14) * mm});
            skLineSegment(sketch, "E84.62.0.0", {"start": v(624.88, 19) * mm, "end": v(624.88, 14) * mm});
            skLineSegment(sketch, "E84.62.0.1", {"start": v(625, 19) * mm, "end": v(625, 14) * mm});
            skLineSegment(sketch, "E84.62.0.2", {"start": v(625.12, 19) * mm, "end": v(625.12, 14) * mm});
            skArc(sketch, "E84.62.0.3", {"start": v(624.88, 19) * mm, "mid": v(625, 19.12) * mm, "end": v(625.13, 19) * mm});
            skArc(sketch, "E84.62.0.4", {"start": v(625.13, 14) * mm, "mid": v(625, 13.88) * mm, "end": v(624.88, 14) * mm});
            skLineSegment(sketch, "E84.63.0.0", {"start": v(634.88, 19) * mm, "end": v(634.88, 14) * mm});
            skLineSegment(sketch, "E84.63.0.1", {"start": v(635, 19) * mm, "end": v(635, 14) * mm});
            skLineSegment(sketch, "E84.63.0.2", {"start": v(635.12, 19) * mm, "end": v(635.12, 14) * mm});
            skArc(sketch, "E84.63.0.3", {"start": v(634.88, 19) * mm, "mid": v(635, 19.12) * mm, "end": v(635.13, 19) * mm});
            skArc(sketch, "E84.63.0.4", {"start": v(635.13, 14) * mm, "mid": v(635, 13.88) * mm, "end": v(634.88, 14) * mm});
            skLineSegment(sketch, "E84.64.0.0", {"start": v(644.88, 19) * mm, "end": v(644.88, 14) * mm});
            skLineSegment(sketch, "E84.64.0.1", {"start": v(645, 19) * mm, "end": v(645, 14) * mm});
            skLineSegment(sketch, "E84.64.0.2", {"start": v(645.13, 19) * mm, "end": v(645.13, 14) * mm});
            skArc(sketch, "E84.64.0.3", {"start": v(644.88, 19) * mm, "mid": v(645, 19.12) * mm, "end": v(645.13, 19) * mm});
            skArc(sketch, "E84.64.0.4", {"start": v(645.13, 14) * mm, "mid": v(645, 13.88) * mm, "end": v(644.88, 14) * mm});
            skLineSegment(sketch, "E84.65.0.0", {"start": v(654.88, 19) * mm, "end": v(654.88, 14) * mm});
            skLineSegment(sketch, "E84.65.0.1", {"start": v(655, 19) * mm, "end": v(655, 14) * mm});
            skLineSegment(sketch, "E84.65.0.2", {"start": v(655.13, 19) * mm, "end": v(655.13, 14) * mm});
            skArc(sketch, "E84.65.0.3", {"start": v(654.88, 19) * mm, "mid": v(655, 19.12) * mm, "end": v(655.13, 19) * mm});
            skArc(sketch, "E84.65.0.4", {"start": v(655.13, 14) * mm, "mid": v(655, 13.88) * mm, "end": v(654.88, 14) * mm});
            skLineSegment(sketch, "E84.66.0.0", {"start": v(664.88, 19) * mm, "end": v(664.88, 14) * mm});
            skLineSegment(sketch, "E84.66.0.1", {"start": v(665, 19) * mm, "end": v(665, 14) * mm});
            skLineSegment(sketch, "E84.66.0.2", {"start": v(665.13, 19) * mm, "end": v(665.13, 14) * mm});
            skArc(sketch, "E84.66.0.3", {"start": v(664.88, 19) * mm, "mid": v(665, 19.12) * mm, "end": v(665.13, 19) * mm});
            skArc(sketch, "E84.66.0.4", {"start": v(665.13, 14) * mm, "mid": v(665, 13.88) * mm, "end": v(664.88, 14) * mm});
            skLineSegment(sketch, "E84.67.0.0", {"start": v(674.88, 19) * mm, "end": v(674.88, 14) * mm});
            skLineSegment(sketch, "E84.67.0.1", {"start": v(675, 19) * mm, "end": v(675, 14) * mm});
            skLineSegment(sketch, "E84.67.0.2", {"start": v(675.13, 19) * mm, "end": v(675.13, 14) * mm});
            skArc(sketch, "E84.67.0.3", {"start": v(674.88, 19) * mm, "mid": v(675, 19.12) * mm, "end": v(675.13, 19) * mm});
            skArc(sketch, "E84.67.0.4", {"start": v(675.13, 14) * mm, "mid": v(675, 13.88) * mm, "end": v(674.88, 14) * mm});
            skLineSegment(sketch, "E84.68.0.0", {"start": v(684.88, 19) * mm, "end": v(684.88, 14) * mm});
            skLineSegment(sketch, "E84.68.0.1", {"start": v(685, 19) * mm, "end": v(685, 14) * mm});
            skLineSegment(sketch, "E84.68.0.2", {"start": v(685.13, 19) * mm, "end": v(685.13, 14) * mm});
            skArc(sketch, "E84.68.0.3", {"start": v(684.88, 19) * mm, "mid": v(685, 19.12) * mm, "end": v(685.13, 19) * mm});
            skArc(sketch, "E84.68.0.4", {"start": v(685.13, 14) * mm, "mid": v(685, 13.88) * mm, "end": v(684.88, 14) * mm});
            skLineSegment(sketch, "E84.69.0.0", {"start": v(694.88, 19) * mm, "end": v(694.88, 14) * mm});
            skLineSegment(sketch, "E84.69.0.1", {"start": v(695, 19) * mm, "end": v(695, 14) * mm});
            skLineSegment(sketch, "E84.69.0.2", {"start": v(695.13, 19) * mm, "end": v(695.13, 14) * mm});
            skArc(sketch, "E84.69.0.3", {"start": v(694.88, 19) * mm, "mid": v(695, 19.12) * mm, "end": v(695.13, 19) * mm});
            skArc(sketch, "E84.69.0.4", {"start": v(695.13, 14) * mm, "mid": v(695, 13.88) * mm, "end": v(694.88, 14) * mm});
            skLineSegment(sketch, "E84.70.0.0", {"start": v(704.88, 19) * mm, "end": v(704.88, 14) * mm});
            skLineSegment(sketch, "E84.70.0.1", {"start": v(705, 19) * mm, "end": v(705, 14) * mm});
            skLineSegment(sketch, "E84.70.0.2", {"start": v(705.13, 19) * mm, "end": v(705.13, 14) * mm});
            skArc(sketch, "E84.70.0.3", {"start": v(704.88, 19) * mm, "mid": v(705, 19.12) * mm, "end": v(705.13, 19) * mm});
            skArc(sketch, "E84.70.0.4", {"start": v(705.13, 14) * mm, "mid": v(705, 13.88) * mm, "end": v(704.88, 14) * mm});
            skLineSegment(sketch, "E84.71.0.0", {"start": v(714.88, 19) * mm, "end": v(714.88, 14) * mm});
            skLineSegment(sketch, "E84.71.0.1", {"start": v(715, 19) * mm, "end": v(715, 14) * mm});
            skLineSegment(sketch, "E84.71.0.2", {"start": v(715.13, 19) * mm, "end": v(715.13, 14) * mm});
            skArc(sketch, "E84.71.0.3", {"start": v(714.88, 19) * mm, "mid": v(715, 19.12) * mm, "end": v(715.13, 19) * mm});
            skArc(sketch, "E84.71.0.4", {"start": v(715.13, 14) * mm, "mid": v(715, 13.88) * mm, "end": v(714.88, 14) * mm});
            skLineSegment(sketch, "E84.72.0.0", {"start": v(724.88, 19) * mm, "end": v(724.88, 14) * mm});
            skLineSegment(sketch, "E84.72.0.1", {"start": v(725, 19) * mm, "end": v(725, 14) * mm});
            skLineSegment(sketch, "E84.72.0.2", {"start": v(725.13, 19) * mm, "end": v(725.13, 14) * mm});
            skArc(sketch, "E84.72.0.3", {"start": v(724.88, 19) * mm, "mid": v(725, 19.12) * mm, "end": v(725.13, 19) * mm});
            skArc(sketch, "E84.72.0.4", {"start": v(725.13, 14) * mm, "mid": v(725, 13.88) * mm, "end": v(724.88, 14) * mm});
            skLineSegment(sketch, "E84.73.0.0", {"start": v(734.88, 19) * mm, "end": v(734.88, 14) * mm});
            skLineSegment(sketch, "E84.73.0.1", {"start": v(735, 19) * mm, "end": v(735, 14) * mm});
            skLineSegment(sketch, "E84.73.0.2", {"start": v(735.12, 19) * mm, "end": v(735.12, 14) * mm});
            skArc(sketch, "E84.73.0.3", {"start": v(734.88, 19) * mm, "mid": v(735, 19.12) * mm, "end": v(735.13, 19) * mm});
            skArc(sketch, "E84.73.0.4", {"start": v(735.13, 14) * mm, "mid": v(735, 13.88) * mm, "end": v(734.88, 14) * mm});
            skLineSegment(sketch, "E84.74.0.0", {"start": v(744.88, 19) * mm, "end": v(744.88, 14) * mm});
            skLineSegment(sketch, "E84.74.0.1", {"start": v(745, 19) * mm, "end": v(745, 14) * mm});
            skLineSegment(sketch, "E84.74.0.2", {"start": v(745.12, 19) * mm, "end": v(745.12, 14) * mm});
            skArc(sketch, "E84.74.0.3", {"start": v(744.88, 19) * mm, "mid": v(745, 19.12) * mm, "end": v(745.13, 19) * mm});
            skArc(sketch, "E84.74.0.4", {"start": v(745.13, 14) * mm, "mid": v(745, 13.88) * mm, "end": v(744.88, 14) * mm});
            skLineSegment(sketch, "E84.75.0.0", {"start": v(754.88, 19) * mm, "end": v(754.88, 14) * mm});
            skLineSegment(sketch, "E84.75.0.1", {"start": v(755, 19) * mm, "end": v(755, 14) * mm});
            skLineSegment(sketch, "E84.75.0.2", {"start": v(755.12, 19) * mm, "end": v(755.12, 14) * mm});
            skArc(sketch, "E84.75.0.3", {"start": v(754.88, 19) * mm, "mid": v(755, 19.12) * mm, "end": v(755.13, 19) * mm});
            skArc(sketch, "E84.75.0.4", {"start": v(755.13, 14) * mm, "mid": v(755, 13.88) * mm, "end": v(754.88, 14) * mm});
            skLineSegment(sketch, "E84.76.0.0", {"start": v(764.88, 19) * mm, "end": v(764.88, 14) * mm});
            skLineSegment(sketch, "E84.76.0.1", {"start": v(765, 19) * mm, "end": v(765, 14) * mm});
            skLineSegment(sketch, "E84.76.0.2", {"start": v(765.12, 19) * mm, "end": v(765.12, 14) * mm});
            skArc(sketch, "E84.76.0.3", {"start": v(764.88, 19) * mm, "mid": v(765, 19.12) * mm, "end": v(765.13, 19) * mm});
            skArc(sketch, "E84.76.0.4", {"start": v(765.13, 14) * mm, "mid": v(765, 13.88) * mm, "end": v(764.88, 14) * mm});
            skLineSegment(sketch, "E84.77.0.0", {"start": v(774.88, 19) * mm, "end": v(774.88, 14) * mm});
            skLineSegment(sketch, "E84.77.0.1", {"start": v(775, 19) * mm, "end": v(775, 14) * mm});
            skLineSegment(sketch, "E84.77.0.2", {"start": v(775.13, 19) * mm, "end": v(775.13, 14) * mm});
            skArc(sketch, "E84.77.0.3", {"start": v(774.88, 19) * mm, "mid": v(775, 19.12) * mm, "end": v(775.13, 19) * mm});
            skArc(sketch, "E84.77.0.4", {"start": v(775.13, 14) * mm, "mid": v(775, 13.88) * mm, "end": v(774.88, 14) * mm});
            skLineSegment(sketch, "E84.78.0.0", {"start": v(784.88, 19) * mm, "end": v(784.88, 14) * mm});
            skLineSegment(sketch, "E84.78.0.1", {"start": v(785, 19) * mm, "end": v(785, 14) * mm});
            skLineSegment(sketch, "E84.78.0.2", {"start": v(785.13, 19) * mm, "end": v(785.13, 14) * mm});
            skArc(sketch, "E84.78.0.3", {"start": v(784.88, 19) * mm, "mid": v(785, 19.12) * mm, "end": v(785.13, 19) * mm});
            skArc(sketch, "E84.78.0.4", {"start": v(785.13, 14) * mm, "mid": v(785, 13.88) * mm, "end": v(784.88, 14) * mm});
            skLineSegment(sketch, "E84.79.0.0", {"start": v(794.88, 19) * mm, "end": v(794.88, 14) * mm});
            skLineSegment(sketch, "E84.79.0.1", {"start": v(795, 19) * mm, "end": v(795, 14) * mm});
            skLineSegment(sketch, "E84.79.0.2", {"start": v(795.13, 19) * mm, "end": v(795.13, 14) * mm});
            skArc(sketch, "E84.79.0.3", {"start": v(794.88, 19) * mm, "mid": v(795, 19.12) * mm, "end": v(795.13, 19) * mm});
            skArc(sketch, "E84.79.0.4", {"start": v(795.13, 14) * mm, "mid": v(795, 13.88) * mm, "end": v(794.88, 14) * mm});
            skLineSegment(sketch, "E84.80.0.0", {"start": v(804.88, 19) * mm, "end": v(804.88, 14) * mm});
            skLineSegment(sketch, "E84.80.0.1", {"start": v(805, 19) * mm, "end": v(805, 14) * mm});
            skLineSegment(sketch, "E84.80.0.2", {"start": v(805.13, 19) * mm, "end": v(805.13, 14) * mm});
            skArc(sketch, "E84.80.0.3", {"start": v(804.88, 19) * mm, "mid": v(805, 19.12) * mm, "end": v(805.13, 19) * mm});
            skArc(sketch, "E84.80.0.4", {"start": v(805.13, 14) * mm, "mid": v(805, 13.88) * mm, "end": v(804.88, 14) * mm});
            skLineSegment(sketch, "E84.81.0.0", {"start": v(814.88, 19) * mm, "end": v(814.88, 14) * mm});
            skLineSegment(sketch, "E84.81.0.1", {"start": v(815, 19) * mm, "end": v(815, 14) * mm});
            skLineSegment(sketch, "E84.81.0.2", {"start": v(815.13, 19) * mm, "end": v(815.13, 14) * mm});
            skArc(sketch, "E84.81.0.3", {"start": v(814.88, 19) * mm, "mid": v(815, 19.12) * mm, "end": v(815.13, 19) * mm});
            skArc(sketch, "E84.81.0.4", {"start": v(815.13, 14) * mm, "mid": v(815, 13.88) * mm, "end": v(814.88, 14) * mm});
            skLineSegment(sketch, "E84.82.0.0", {"start": v(824.88, 19) * mm, "end": v(824.88, 14) * mm});
            skLineSegment(sketch, "E84.82.0.1", {"start": v(825, 19) * mm, "end": v(825, 14) * mm});
            skLineSegment(sketch, "E84.82.0.2", {"start": v(825.13, 19) * mm, "end": v(825.13, 14) * mm});
            skArc(sketch, "E84.82.0.3", {"start": v(824.88, 19) * mm, "mid": v(825, 19.12) * mm, "end": v(825.13, 19) * mm});
            skArc(sketch, "E84.82.0.4", {"start": v(825.13, 14) * mm, "mid": v(825, 13.88) * mm, "end": v(824.88, 14) * mm});
            skLineSegment(sketch, "E84.83.0.0", {"start": v(834.88, 19) * mm, "end": v(834.88, 14) * mm});
            skLineSegment(sketch, "E84.83.0.1", {"start": v(835, 19) * mm, "end": v(835, 14) * mm});
            skLineSegment(sketch, "E84.83.0.2", {"start": v(835.13, 19) * mm, "end": v(835.13, 14) * mm});
            skArc(sketch, "E84.83.0.3", {"start": v(834.88, 19) * mm, "mid": v(835, 19.12) * mm, "end": v(835.13, 19) * mm});
            skArc(sketch, "E84.83.0.4", {"start": v(835.13, 14) * mm, "mid": v(835, 13.88) * mm, "end": v(834.88, 14) * mm});
            skLineSegment(sketch, "E84.84.0.0", {"start": v(844.88, 19) * mm, "end": v(844.88, 14) * mm});
            skLineSegment(sketch, "E84.84.0.1", {"start": v(845, 19) * mm, "end": v(845, 14) * mm});
            skLineSegment(sketch, "E84.84.0.2", {"start": v(845.13, 19) * mm, "end": v(845.13, 14) * mm});
            skArc(sketch, "E84.84.0.3", {"start": v(844.88, 19) * mm, "mid": v(845, 19.12) * mm, "end": v(845.13, 19) * mm});
            skArc(sketch, "E84.84.0.4", {"start": v(845.13, 14) * mm, "mid": v(845, 13.88) * mm, "end": v(844.88, 14) * mm});
            skLineSegment(sketch, "E84.85.0.0", {"start": v(854.88, 19) * mm, "end": v(854.88, 14) * mm});
            skLineSegment(sketch, "E84.85.0.1", {"start": v(855, 19) * mm, "end": v(855, 14) * mm});
            skLineSegment(sketch, "E84.85.0.2", {"start": v(855.13, 19) * mm, "end": v(855.13, 14) * mm});
            skArc(sketch, "E84.85.0.3", {"start": v(854.88, 19) * mm, "mid": v(855, 19.12) * mm, "end": v(855.13, 19) * mm});
            skArc(sketch, "E84.85.0.4", {"start": v(855.13, 14) * mm, "mid": v(855, 13.88) * mm, "end": v(854.88, 14) * mm});
            skLineSegment(sketch, "E84.86.0.0", {"start": v(864.88, 19) * mm, "end": v(864.88, 14) * mm});
            skLineSegment(sketch, "E84.86.0.1", {"start": v(865, 19) * mm, "end": v(865, 14) * mm});
            skLineSegment(sketch, "E84.86.0.2", {"start": v(865.13, 19) * mm, "end": v(865.13, 14) * mm});
            skArc(sketch, "E84.86.0.3", {"start": v(864.88, 19) * mm, "mid": v(865, 19.12) * mm, "end": v(865.13, 19) * mm});
            skArc(sketch, "E84.86.0.4", {"start": v(865.13, 14) * mm, "mid": v(865, 13.88) * mm, "end": v(864.88, 14) * mm});
            skLineSegment(sketch, "E84.87.0.0", {"start": v(874.88, 19) * mm, "end": v(874.88, 14) * mm});
            skLineSegment(sketch, "E84.87.0.1", {"start": v(875, 19) * mm, "end": v(875, 14) * mm});
            skLineSegment(sketch, "E84.87.0.2", {"start": v(875.13, 19) * mm, "end": v(875.13, 14) * mm});
            skArc(sketch, "E84.87.0.3", {"start": v(874.88, 19) * mm, "mid": v(875, 19.12) * mm, "end": v(875.13, 19) * mm});
            skArc(sketch, "E84.87.0.4", {"start": v(875.13, 14) * mm, "mid": v(875, 13.88) * mm, "end": v(874.88, 14) * mm});
            skLineSegment(sketch, "E84.88.0.0", {"start": v(884.88, 19) * mm, "end": v(884.88, 14) * mm});
            skLineSegment(sketch, "E84.88.0.1", {"start": v(885, 19) * mm, "end": v(885, 14) * mm});
            skLineSegment(sketch, "E84.88.0.2", {"start": v(885.12, 19) * mm, "end": v(885.12, 14) * mm});
            skArc(sketch, "E84.88.0.3", {"start": v(884.88, 19) * mm, "mid": v(885, 19.12) * mm, "end": v(885.13, 19) * mm});
            skArc(sketch, "E84.88.0.4", {"start": v(885.13, 14) * mm, "mid": v(885, 13.88) * mm, "end": v(884.88, 14) * mm});
            skLineSegment(sketch, "E84.89.0.0", {"start": v(894.88, 19) * mm, "end": v(894.88, 14) * mm});
            skLineSegment(sketch, "E84.89.0.1", {"start": v(895, 19) * mm, "end": v(895, 14) * mm});
            skLineSegment(sketch, "E84.89.0.2", {"start": v(895.13, 19) * mm, "end": v(895.13, 14) * mm});
            skArc(sketch, "E84.89.0.3", {"start": v(894.88, 19) * mm, "mid": v(895, 19.12) * mm, "end": v(895.13, 19) * mm});
            skArc(sketch, "E84.89.0.4", {"start": v(895.13, 14) * mm, "mid": v(895, 13.88) * mm, "end": v(894.88, 14) * mm});
            skLineSegment(sketch, "E84.90.0.0", {"start": v(904.88, 19) * mm, "end": v(904.88, 14) * mm});
            skLineSegment(sketch, "E84.90.0.1", {"start": v(905, 19) * mm, "end": v(905, 14) * mm});
            skLineSegment(sketch, "E84.90.0.2", {"start": v(905.13, 19) * mm, "end": v(905.13, 14) * mm});
            skArc(sketch, "E84.90.0.3", {"start": v(904.88, 19) * mm, "mid": v(905, 19.12) * mm, "end": v(905.13, 19) * mm});
            skArc(sketch, "E84.90.0.4", {"start": v(905.13, 14) * mm, "mid": v(905, 13.88) * mm, "end": v(904.88, 14) * mm});
            skLineSegment(sketch, "E84.91.0.0", {"start": v(914.88, 19) * mm, "end": v(914.88, 14) * mm});
            skLineSegment(sketch, "E84.91.0.1", {"start": v(915, 19) * mm, "end": v(915, 14) * mm});
            skLineSegment(sketch, "E84.91.0.2", {"start": v(915.13, 19) * mm, "end": v(915.13, 14) * mm});
            skArc(sketch, "E84.91.0.3", {"start": v(914.88, 19) * mm, "mid": v(915, 19.12) * mm, "end": v(915.13, 19) * mm});
            skArc(sketch, "E84.91.0.4", {"start": v(915.13, 14) * mm, "mid": v(915, 13.88) * mm, "end": v(914.88, 14) * mm});
            skLineSegment(sketch, "E84.92.0.0", {"start": v(924.88, 19) * mm, "end": v(924.88, 14) * mm});
            skLineSegment(sketch, "E84.92.0.1", {"start": v(925, 19) * mm, "end": v(925, 14) * mm});
            skLineSegment(sketch, "E84.92.0.2", {"start": v(925.13, 19) * mm, "end": v(925.13, 14) * mm});
            skArc(sketch, "E84.92.0.3", {"start": v(924.88, 19) * mm, "mid": v(925, 19.12) * mm, "end": v(925.13, 19) * mm});
            skArc(sketch, "E84.92.0.4", {"start": v(925.13, 14) * mm, "mid": v(925, 13.88) * mm, "end": v(924.88, 14) * mm});
            skLineSegment(sketch, "E84.93.0.0", {"start": v(934.88, 19) * mm, "end": v(934.88, 14) * mm});
            skLineSegment(sketch, "E84.93.0.1", {"start": v(935, 19) * mm, "end": v(935, 14) * mm});
            skLineSegment(sketch, "E84.93.0.2", {"start": v(935.13, 19) * mm, "end": v(935.13, 14) * mm});
            skArc(sketch, "E84.93.0.3", {"start": v(934.88, 19) * mm, "mid": v(935, 19.12) * mm, "end": v(935.13, 19) * mm});
            skArc(sketch, "E84.93.0.4", {"start": v(935.13, 14) * mm, "mid": v(935, 13.88) * mm, "end": v(934.88, 14) * mm});
            skLineSegment(sketch, "E84.94.0.0", {"start": v(944.88, 19) * mm, "end": v(944.88, 14) * mm});
            skLineSegment(sketch, "E84.94.0.1", {"start": v(945, 19) * mm, "end": v(945, 14) * mm});
            skLineSegment(sketch, "E84.94.0.2", {"start": v(945.13, 19) * mm, "end": v(945.13, 14) * mm});
            skArc(sketch, "E84.94.0.3", {"start": v(944.88, 19) * mm, "mid": v(945, 19.12) * mm, "end": v(945.13, 19) * mm});
            skArc(sketch, "E84.94.0.4", {"start": v(945.13, 14) * mm, "mid": v(945, 13.88) * mm, "end": v(944.88, 14) * mm});
            skLineSegment(sketch, "E84.95.0.0", {"start": v(954.88, 19) * mm, "end": v(954.88, 14) * mm});
            skLineSegment(sketch, "E84.95.0.1", {"start": v(955, 19) * mm, "end": v(955, 14) * mm});
            skLineSegment(sketch, "E84.95.0.2", {"start": v(955.13, 19) * mm, "end": v(955.13, 14) * mm});
            skArc(sketch, "E84.95.0.3", {"start": v(954.88, 19) * mm, "mid": v(955, 19.12) * mm, "end": v(955.13, 19) * mm});
            skArc(sketch, "E84.95.0.4", {"start": v(955.13, 14) * mm, "mid": v(955, 13.88) * mm, "end": v(954.88, 14) * mm});
            skLineSegment(sketch, "E84.96.0.0", {"start": v(964.88, 19) * mm, "end": v(964.88, 14) * mm});
            skLineSegment(sketch, "E84.96.0.1", {"start": v(965, 19) * mm, "end": v(965, 14) * mm});
            skLineSegment(sketch, "E84.96.0.2", {"start": v(965.13, 19) * mm, "end": v(965.13, 14) * mm});
            skArc(sketch, "E84.96.0.3", {"start": v(964.88, 19) * mm, "mid": v(965, 19.12) * mm, "end": v(965.13, 19) * mm});
            skArc(sketch, "E84.96.0.4", {"start": v(965.13, 14) * mm, "mid": v(965, 13.88) * mm, "end": v(964.88, 14) * mm});
            skLineSegment(sketch, "E84.97.0.0", {"start": v(974.88, 19) * mm, "end": v(974.88, 14) * mm});
            skLineSegment(sketch, "E84.97.0.1", {"start": v(975, 19) * mm, "end": v(975, 14) * mm});
            skLineSegment(sketch, "E84.97.0.2", {"start": v(975.13, 19) * mm, "end": v(975.13, 14) * mm});
            skArc(sketch, "E84.97.0.3", {"start": v(974.88, 19) * mm, "mid": v(975, 19.12) * mm, "end": v(975.13, 19) * mm});
            skArc(sketch, "E84.97.0.4", {"start": v(975.13, 14) * mm, "mid": v(975, 13.88) * mm, "end": v(974.88, 14) * mm});
            skLineSegment(sketch, "E84.98.0.0", {"start": v(984.88, 19) * mm, "end": v(984.88, 14) * mm});
            skLineSegment(sketch, "E84.98.0.1", {"start": v(985, 19) * mm, "end": v(985, 14) * mm});
            skLineSegment(sketch, "E84.98.0.2", {"start": v(985.13, 19) * mm, "end": v(985.13, 14) * mm});
            skArc(sketch, "E84.98.0.3", {"start": v(984.88, 19) * mm, "mid": v(985, 19.12) * mm, "end": v(985.13, 19) * mm});
            skArc(sketch, "E84.98.0.4", {"start": v(985.13, 14) * mm, "mid": v(985, 13.88) * mm, "end": v(984.88, 14) * mm});
            skLineSegment(sketch, "E84.99.0.0", {"start": v(994.88, 19) * mm, "end": v(994.88, 14) * mm});
            skLineSegment(sketch, "E84.99.0.1", {"start": v(995, 19) * mm, "end": v(995, 14) * mm});
            skLineSegment(sketch, "E84.99.0.2", {"start": v(995.13, 19) * mm, "end": v(995.13, 14) * mm});
            skArc(sketch, "E84.99.0.3", {"start": v(994.88, 19) * mm, "mid": v(995, 19.12) * mm, "end": v(995.13, 19) * mm});
            skArc(sketch, "E84.99.0.4", {"start": v(995.13, 14) * mm, "mid": v(995, 13.88) * mm, "end": v(994.88, 14) * mm});
            skLineSegment(sketch, "E84.direction1", {"start": v(4.88, 14) * mm, "end": v(14.88, 14) * mm, "construction": true});
            skLineSegment(sketch, "E85.1.0.0", {"start": v(1005.12, 19) * mm, "end": v(1005.12, 14) * mm});
            skArc(sketch, "E85.1.0.1", {"start": v(1005.13, 14) * mm, "mid": v(1005, 13.88) * mm, "end": v(1004.88, 14) * mm});
            skLineSegment(sketch, "E85.1.0.2", {"start": v(1004.88, 19) * mm, "end": v(1004.88, 14) * mm});
            skLineSegment(sketch, "E85.1.0.3", {"start": v(1005, 19) * mm, "end": v(1005, 14) * mm});
            skArc(sketch, "E85.1.0.4", {"start": v(1004.88, 19) * mm, "mid": v(1005, 19.12) * mm, "end": v(1005.13, 19) * mm});
            skLineSegment(sketch, "E85.2.0.0", {"start": v(1015.12, 19) * mm, "end": v(1015.12, 14) * mm});
            skArc(sketch, "E85.2.0.1", {"start": v(1015.12, 14) * mm, "mid": v(1015, 13.88) * mm, "end": v(1014.88, 14) * mm});
            skLineSegment(sketch, "E85.2.0.2", {"start": v(1014.88, 19) * mm, "end": v(1014.88, 14) * mm});
            skLineSegment(sketch, "E85.2.0.3", {"start": v(1015, 19) * mm, "end": v(1015, 14) * mm});
            skArc(sketch, "E85.2.0.4", {"start": v(1014.88, 19) * mm, "mid": v(1015, 19.12) * mm, "end": v(1015.12, 19) * mm});
            skLineSegment(sketch, "E85.3.0.0", {"start": v(1025.12, 19) * mm, "end": v(1025.12, 14) * mm});
            skArc(sketch, "E85.3.0.1", {"start": v(1025.12, 14) * mm, "mid": v(1025, 13.88) * mm, "end": v(1024.88, 14) * mm});
            skLineSegment(sketch, "E85.3.0.2", {"start": v(1024.88, 19) * mm, "end": v(1024.88, 14) * mm});
            skLineSegment(sketch, "E85.3.0.3", {"start": v(1025, 19) * mm, "end": v(1025, 14) * mm});
            skArc(sketch, "E85.3.0.4", {"start": v(1024.88, 19) * mm, "mid": v(1025, 19.12) * mm, "end": v(1025.12, 19) * mm});
            skLineSegment(sketch, "E85.4.0.0", {"start": v(1035.12, 19) * mm, "end": v(1035.12, 14) * mm});
            skArc(sketch, "E85.4.0.1", {"start": v(1035.12, 14) * mm, "mid": v(1035, 13.88) * mm, "end": v(1034.88, 14) * mm});
            skLineSegment(sketch, "E85.4.0.2", {"start": v(1034.88, 19) * mm, "end": v(1034.88, 14) * mm});
            skLineSegment(sketch, "E85.4.0.3", {"start": v(1035, 19) * mm, "end": v(1035, 14) * mm});
            skArc(sketch, "E85.4.0.4", {"start": v(1034.88, 19) * mm, "mid": v(1035, 19.12) * mm, "end": v(1035.12, 19) * mm});
            skLineSegment(sketch, "E85.5.0.0", {"start": v(1045.12, 19) * mm, "end": v(1045.12, 14) * mm});
            skArc(sketch, "E85.5.0.1", {"start": v(1045.12, 14) * mm, "mid": v(1045, 13.88) * mm, "end": v(1044.88, 14) * mm});
            skLineSegment(sketch, "E85.5.0.2", {"start": v(1044.87, 19) * mm, "end": v(1044.87, 14) * mm});
            skLineSegment(sketch, "E85.5.0.3", {"start": v(1045, 19) * mm, "end": v(1045, 14) * mm});
            skArc(sketch, "E85.5.0.4", {"start": v(1044.88, 19) * mm, "mid": v(1045, 19.12) * mm, "end": v(1045.12, 19) * mm});
            skLineSegment(sketch, "E85.6.0.0", {"start": v(1055.12, 19) * mm, "end": v(1055.12, 14) * mm});
            skArc(sketch, "E85.6.0.1", {"start": v(1055.12, 14) * mm, "mid": v(1055, 13.88) * mm, "end": v(1054.87, 14) * mm});
            skLineSegment(sketch, "E85.6.0.2", {"start": v(1054.87, 19) * mm, "end": v(1054.87, 14) * mm});
            skLineSegment(sketch, "E85.6.0.3", {"start": v(1055, 19) * mm, "end": v(1055, 14) * mm});
            skArc(sketch, "E85.6.0.4", {"start": v(1054.87, 19) * mm, "mid": v(1055, 19.12) * mm, "end": v(1055.12, 19) * mm});
            skLineSegment(sketch, "E85.7.0.0", {"start": v(1065.12, 19) * mm, "end": v(1065.12, 14) * mm});
            skArc(sketch, "E85.7.0.1", {"start": v(1065.12, 14) * mm, "mid": v(1065, 13.88) * mm, "end": v(1064.87, 14) * mm});
            skLineSegment(sketch, "E85.7.0.2", {"start": v(1064.87, 19) * mm, "end": v(1064.87, 14) * mm});
            skLineSegment(sketch, "E85.7.0.3", {"start": v(1065, 19) * mm, "end": v(1065, 14) * mm});
            skArc(sketch, "E85.7.0.4", {"start": v(1064.87, 19) * mm, "mid": v(1065, 19.12) * mm, "end": v(1065.12, 19) * mm});
            skLineSegment(sketch, "E85.8.0.0", {"start": v(1075.12, 19) * mm, "end": v(1075.12, 14) * mm});
            skArc(sketch, "E85.8.0.1", {"start": v(1075.12, 14) * mm, "mid": v(1075, 13.88) * mm, "end": v(1074.87, 14) * mm});
            skLineSegment(sketch, "E85.8.0.2", {"start": v(1074.87, 19) * mm, "end": v(1074.87, 14) * mm});
            skLineSegment(sketch, "E85.8.0.3", {"start": v(1075, 19) * mm, "end": v(1075, 14) * mm});
            skArc(sketch, "E85.8.0.4", {"start": v(1074.87, 19) * mm, "mid": v(1075, 19.12) * mm, "end": v(1075.12, 19) * mm});
            skLineSegment(sketch, "E85.9.0.0", {"start": v(1085.12, 19) * mm, "end": v(1085.12, 14) * mm});
            skArc(sketch, "E85.9.0.1", {"start": v(1085.12, 14) * mm, "mid": v(1085, 13.88) * mm, "end": v(1084.87, 14) * mm});
            skLineSegment(sketch, "E85.9.0.2", {"start": v(1084.87, 19) * mm, "end": v(1084.87, 14) * mm});
            skLineSegment(sketch, "E85.9.0.3", {"start": v(1085, 19) * mm, "end": v(1085, 14) * mm});
            skArc(sketch, "E85.9.0.4", {"start": v(1084.87, 19) * mm, "mid": v(1085, 19.12) * mm, "end": v(1085.12, 19) * mm});
            skLineSegment(sketch, "E85.10.0.0", {"start": v(1095.12, 19) * mm, "end": v(1095.12, 14) * mm});
            skArc(sketch, "E85.10.0.1", {"start": v(1095.12, 14) * mm, "mid": v(1095, 13.88) * mm, "end": v(1094.87, 14) * mm});
            skLineSegment(sketch, "E85.10.0.2", {"start": v(1094.87, 19) * mm, "end": v(1094.87, 14) * mm});
            skLineSegment(sketch, "E85.10.0.3", {"start": v(1095, 19) * mm, "end": v(1095, 14) * mm});
            skArc(sketch, "E85.10.0.4", {"start": v(1094.87, 19) * mm, "mid": v(1095, 19.12) * mm, "end": v(1095.12, 19) * mm});
            skLineSegment(sketch, "E85.11.0.0", {"start": v(1105.12, 19) * mm, "end": v(1105.12, 14) * mm});
            skArc(sketch, "E85.11.0.1", {"start": v(1105.12, 14) * mm, "mid": v(1105, 13.88) * mm, "end": v(1104.87, 14) * mm});
            skLineSegment(sketch, "E85.11.0.2", {"start": v(1104.87, 19) * mm, "end": v(1104.87, 14) * mm});
            skLineSegment(sketch, "E85.11.0.3", {"start": v(1105, 19) * mm, "end": v(1105, 14) * mm});
            skArc(sketch, "E85.11.0.4", {"start": v(1104.87, 19) * mm, "mid": v(1105, 19.12) * mm, "end": v(1105.12, 19) * mm});
            skLineSegment(sketch, "E85.12.0.0", {"start": v(1115.12, 19) * mm, "end": v(1115.12, 14) * mm});
            skArc(sketch, "E85.12.0.1", {"start": v(1115.12, 14) * mm, "mid": v(1115, 13.88) * mm, "end": v(1114.87, 14) * mm});
            skLineSegment(sketch, "E85.12.0.2", {"start": v(1114.87, 19) * mm, "end": v(1114.87, 14) * mm});
            skLineSegment(sketch, "E85.12.0.3", {"start": v(1115, 19) * mm, "end": v(1115, 14) * mm});
            skArc(sketch, "E85.12.0.4", {"start": v(1114.87, 19) * mm, "mid": v(1115, 19.12) * mm, "end": v(1115.12, 19) * mm});
            skLineSegment(sketch, "E85.13.0.0", {"start": v(1125.12, 19) * mm, "end": v(1125.12, 14) * mm});
            skArc(sketch, "E85.13.0.1", {"start": v(1125.12, 14) * mm, "mid": v(1125, 13.88) * mm, "end": v(1124.87, 14) * mm});
            skLineSegment(sketch, "E85.13.0.2", {"start": v(1124.87, 19) * mm, "end": v(1124.87, 14) * mm});
            skLineSegment(sketch, "E85.13.0.3", {"start": v(1125, 19) * mm, "end": v(1125, 14) * mm});
            skArc(sketch, "E85.13.0.4", {"start": v(1124.87, 19) * mm, "mid": v(1125, 19.12) * mm, "end": v(1125.12, 19) * mm});
            skLineSegment(sketch, "E85.14.0.0", {"start": v(1135.12, 19) * mm, "end": v(1135.12, 14) * mm});
            skArc(sketch, "E85.14.0.1", {"start": v(1135.12, 14) * mm, "mid": v(1135, 13.88) * mm, "end": v(1134.87, 14) * mm});
            skLineSegment(sketch, "E85.14.0.2", {"start": v(1134.87, 19) * mm, "end": v(1134.87, 14) * mm});
            skLineSegment(sketch, "E85.14.0.3", {"start": v(1135, 19) * mm, "end": v(1135, 14) * mm});
            skArc(sketch, "E85.14.0.4", {"start": v(1134.87, 19) * mm, "mid": v(1135, 19.12) * mm, "end": v(1135.12, 19) * mm});
            skLineSegment(sketch, "E85.15.0.0", {"start": v(1145.12, 19) * mm, "end": v(1145.12, 14) * mm});
            skArc(sketch, "E85.15.0.1", {"start": v(1145.12, 14) * mm, "mid": v(1145, 13.88) * mm, "end": v(1144.87, 14) * mm});
            skLineSegment(sketch, "E85.15.0.2", {"start": v(1144.87, 19) * mm, "end": v(1144.87, 14) * mm});
            skLineSegment(sketch, "E85.15.0.3", {"start": v(1145, 19) * mm, "end": v(1145, 14) * mm});
            skArc(sketch, "E85.15.0.4", {"start": v(1144.87, 19) * mm, "mid": v(1145, 19.12) * mm, "end": v(1145.12, 19) * mm});
            skLineSegment(sketch, "E85.16.0.0", {"start": v(1155.12, 19) * mm, "end": v(1155.12, 14) * mm});
            skArc(sketch, "E85.16.0.1", {"start": v(1155.12, 14) * mm, "mid": v(1155, 13.88) * mm, "end": v(1154.87, 14) * mm});
            skLineSegment(sketch, "E85.16.0.2", {"start": v(1154.87, 19) * mm, "end": v(1154.87, 14) * mm});
            skLineSegment(sketch, "E85.16.0.3", {"start": v(1155, 19) * mm, "end": v(1155, 14) * mm});
            skArc(sketch, "E85.16.0.4", {"start": v(1154.87, 19) * mm, "mid": v(1155, 19.12) * mm, "end": v(1155.12, 19) * mm});
            skLineSegment(sketch, "E85.17.0.0", {"start": v(1165.12, 19) * mm, "end": v(1165.12, 14) * mm});
            skArc(sketch, "E85.17.0.1", {"start": v(1165.12, 14) * mm, "mid": v(1165, 13.88) * mm, "end": v(1164.87, 14) * mm});
            skLineSegment(sketch, "E85.17.0.2", {"start": v(1164.87, 19) * mm, "end": v(1164.87, 14) * mm});
            skLineSegment(sketch, "E85.17.0.3", {"start": v(1165, 19) * mm, "end": v(1165, 14) * mm});
            skArc(sketch, "E85.17.0.4", {"start": v(1164.87, 19) * mm, "mid": v(1165, 19.12) * mm, "end": v(1165.12, 19) * mm});
            skLineSegment(sketch, "E85.18.0.0", {"start": v(1175.12, 19) * mm, "end": v(1175.12, 14) * mm});
            skArc(sketch, "E85.18.0.1", {"start": v(1175.12, 14) * mm, "mid": v(1175, 13.88) * mm, "end": v(1174.87, 14) * mm});
            skLineSegment(sketch, "E85.18.0.2", {"start": v(1174.87, 19) * mm, "end": v(1174.87, 14) * mm});
            skLineSegment(sketch, "E85.18.0.3", {"start": v(1175, 19) * mm, "end": v(1175, 14) * mm});
            skArc(sketch, "E85.18.0.4", {"start": v(1174.87, 19) * mm, "mid": v(1175, 19.12) * mm, "end": v(1175.12, 19) * mm});
            skLineSegment(sketch, "E85.direction1", {"start": v(994.88, 14) * mm, "end": v(1004.88, 14) * mm, "construction": true});
            skSolve(sketch);
        }
        {
            var Q0;
            Q0 = qSketchRegion(id + "F15", true);
            extrude(context, id + "F16", {"entities" : qUnion([Q0]), "operationType" : NewBodyOperationType.REMOVE, "oppositeDirection" : true, "depth" : 0.25 * mm, "offsetDistance" : 25 * mm});
        }
    });
